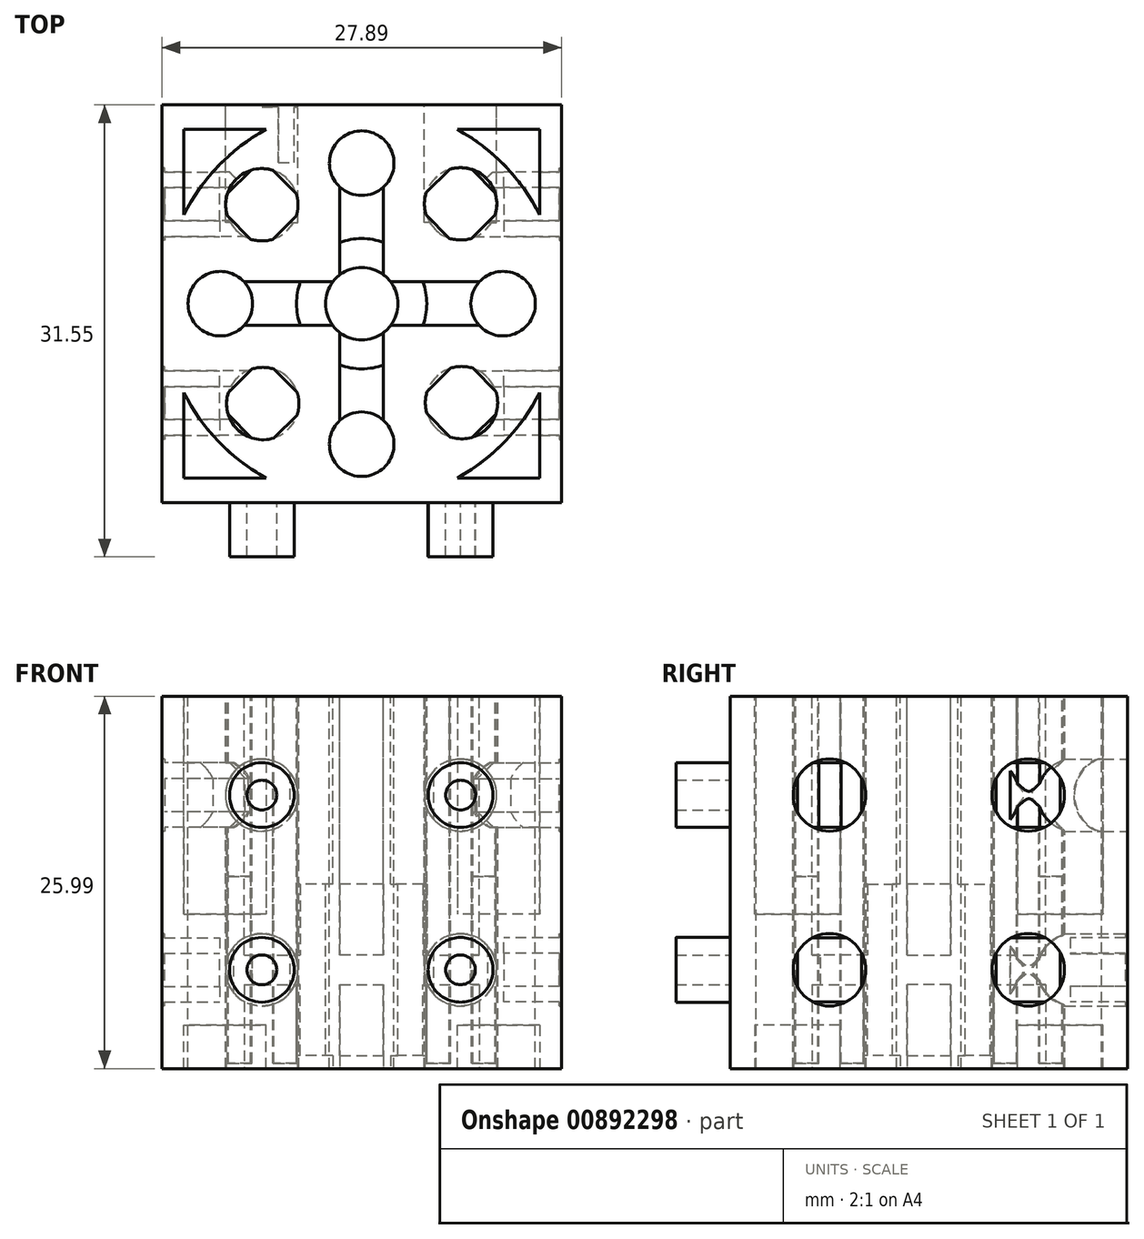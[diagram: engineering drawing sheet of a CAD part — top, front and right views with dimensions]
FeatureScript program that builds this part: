
annotation { "Feature Type Name" : "Feature", "Feature Type Description" : "" }
export const myFeature = defineFeature(function(context is Context, id is Id, definition is map)
    precondition{}
    {
        {
            var Q0;
            Q0=qCreatedBy(makeId("Top.planeOp"),FACE);
            var sketch = newSketch(context, id + "F0", { "sketchPlane" : qUnion([Q0])});
            skLineSegment(sketch, "E0.bottom", {"start": v(-12.61, 9.27) * mm, "end": v(15.28, 9.27) * mm});
            skLineSegment(sketch, "E0.top", {"start": v(-12.61, -18.5) * mm, "end": v(15.28, -18.5) * mm});
            skLineSegment(sketch, "E0.left", {"start": v(-12.61, 9.27) * mm, "end": v(-12.61, -18.5) * mm});
            skLineSegment(sketch, "E0.right", {"start": v(15.28, 9.27) * mm, "end": v(15.28, -18.5) * mm});
            skSolve(sketch);
        }
        {
            var Q0;
            Q0=qSketchRegion(id+"F0",true);
            extrude(context, id + "F1", {"entities" : qUnion([Q0]), "depth" : 13.8 * mm, "offsetDistance" : 25.4 * mm});
        }
        {
            var Q0;
            Q0=makeQuery(id+"F1.opExtrude","CAP_FACE",FACE,{"disambiguationData":[OSD([sQuery(id+"F0.wireOp",EDGE,"E0.bottom"),sQuery(id+"F0.wireOp",EDGE,"E0.top"),sQuery(id+"F0.wireOp",EDGE,"E0.left"),sQuery(id+"F0.wireOp",EDGE,"E0.right")])],"isStart":false});
            var sketch = newSketch(context, id + "F2", { "sketchPlane" : qUnion([Q0])});
            skLineSegment(sketch, "E1", {"start": v(1.33, 9.27) * mm, "end": v(1.33, -18.5) * mm, "construction": true});
            skLineSegment(sketch, "E2", {"start": v(-12.61, -4.61) * mm, "end": v(15.28, -4.61) * mm, "construction": true});
            skLineSegment(sketch, "E3.bottom", {"start": v(13.75, 7.56) * mm, "end": v(-11.09, 7.56) * mm});
            skLineSegment(sketch, "E3.top", {"start": v(13.75, -16.78) * mm, "end": v(-11.09, -16.78) * mm});
            skLineSegment(sketch, "E3.left", {"start": v(13.75, 7.56) * mm, "end": v(13.75, -16.78) * mm});
            skLineSegment(sketch, "E3.right", {"start": v(-11.09, 7.56) * mm, "end": v(-11.09, -16.78) * mm});
            skPoint(sketch, "E3.middle", {"position": v(1.33, -4.61) * mm});
            skSolve(sketch);
        }
        {
            var Q0;
            Q0=qSketchRegion(id+"F2",true);
            extrude(context, id + "F3", {"entities" : qUnion([Q0]), "operationType" : NewBodyOperationType.REMOVE, "oppositeDirection" : true, "depth" : 3.02 * mm, "offsetDistance" : 25.4 * mm});
        }
        {
            var Q0;
            Q0=makeQuery(id+"F1.opExtrude","CAP_FACE",FACE,{"disambiguationData":[OSD([sQuery(id+"F0.wireOp",EDGE,"E0.bottom"),sQuery(id+"F0.wireOp",EDGE,"E0.top"),sQuery(id+"F0.wireOp",EDGE,"E0.left"),sQuery(id+"F0.wireOp",EDGE,"E0.right")])],"isStart":true});
            var sketch = newSketch(context, id + "F4", { "sketchPlane" : qUnion([Q0])});
            skLineSegment(sketch, "E4.bottom", {"start": v(-11.09, -7.56) * mm, "end": v(13.75, -7.56) * mm});
            skLineSegment(sketch, "E4.top", {"start": v(-11.09, 16.78) * mm, "end": v(13.75, 16.78) * mm});
            skLineSegment(sketch, "E4.left", {"start": v(-11.09, -7.56) * mm, "end": v(-11.09, 16.78) * mm});
            skLineSegment(sketch, "E4.right", {"start": v(13.75, -7.56) * mm, "end": v(13.75, 16.78) * mm});
            skSolve(sketch);
        }
        {
            var Q0;
            Q0=makeQuery(id+"F4.imprint","IMPRINT",FACE,{"disambiguationData":[TD([[makeQuery(id+"F4.imprint","IMPRINT",EDGE,{"derivedFrom":sQuery(id+"F4.wireOp",EDGE,"E4.bottom")}),1.0]])]});
            extrude(context, id + "F5", {"entities" : qUnion([Q0]), "operationType" : NewBodyOperationType.REMOVE, "oppositeDirection" : true, "depth" : 3.02 * mm, "offsetDistance" : 25.4 * mm});
        }
        {
            var Q0;
            Q0=makeQuery(id+"F5.boolean.opBoolean","COPY",FACE,{"derivedFrom":makeQuery(id+"F5.opExtrude","CAP_FACE",FACE,{"disambiguationData":[OSD([sQuery(id+"F4.wireOp",EDGE,"E4.bottom"),sQuery(id+"F4.wireOp",EDGE,"E4.top"),sQuery(id+"F4.wireOp",EDGE,"E4.left"),sQuery(id+"F4.wireOp",EDGE,"E4.right")])],"isStart":false})});
            var sketch = newSketch(context, id + "F6", { "sketchPlane" : qUnion([Q0])});
            skCircle(sketch, "E5", {"center": v(1.33, 4.61) * mm, "radius": 13.88 * mm});
            skLineSegment(sketch, "E6", {"start": v(1.33, -7.56) * mm, "end": v(1.33, 16.78) * mm, "construction": true});
            skPoint(sketch, "E6.startSnap0", {"position": v(1.33, -7.56) * mm});
            skSolve(sketch);
        }
        {
            var Q0;
            {var subQ0=sQuery(id+"F6.wireOp",EDGE,"E5");var subQ1=makeQuery(id+"F5.boolean.opBoolean","COPY",EDGE,{"derivedFrom":makeQuery(id+"F5.opExtrude","CAP_EDGE",EDGE,{"disambiguationData":[OSD([sQuery(id+"F4.wireOp",EDGE,"E4.top")])],"isStart":false})});var subQ2=makeQuery(id+"F6.imprint","INTERSECT",VERTEX,{"disambiguationData":[OD(0.0)],"derivedFrom":[subQ1,subQ0]});Q0=makeQuery(id+"F6.imprint","IMPRINT",FACE,{"disambiguationData":[TD([[makeQuery(id+"F6.imprint","IMPRINT",EDGE,{"disambiguationData":[TD([[subQ2,-1.0]])],"derivedFrom":subQ0}),1.0]])]});}
            var Q1;
            {var subQ0=sQuery(id+"F6.wireOp",EDGE,"E5");var subQ1=makeQuery(id+"F5.boolean.opBoolean","COPY",EDGE,{"derivedFrom":makeQuery(id+"F5.opExtrude","CAP_EDGE",EDGE,{"disambiguationData":[OSD([sQuery(id+"F4.wireOp",EDGE,"E4.left")])],"isStart":false})});var subQ2=makeQuery(id+"F6.imprint","INTERSECT",VERTEX,{"disambiguationData":[OD(0.0)],"derivedFrom":[subQ1,subQ0]});Q1=makeQuery(id+"F6.imprint","IMPRINT",FACE,{"disambiguationData":[TD([[makeQuery(id+"F6.imprint","IMPRINT",EDGE,{"disambiguationData":[TD([[subQ2,-1.0]])],"derivedFrom":subQ0}),1.0]])]});}
            var Q2;
            {var subQ0=sQuery(id+"F6.wireOp",EDGE,"E5");var subQ1=makeQuery(id+"F5.boolean.opBoolean","COPY",EDGE,{"derivedFrom":makeQuery(id+"F5.opExtrude","CAP_EDGE",EDGE,{"disambiguationData":[OSD([sQuery(id+"F4.wireOp",EDGE,"E4.bottom")])],"isStart":false})});var subQ2=makeQuery(id+"F6.imprint","INTERSECT",VERTEX,{"disambiguationData":[OD(0.0)],"derivedFrom":[subQ1,subQ0]});Q2=makeQuery(id+"F6.imprint","IMPRINT",FACE,{"disambiguationData":[TD([[makeQuery(id+"F6.imprint","IMPRINT",EDGE,{"disambiguationData":[TD([[subQ2,-1.0]])],"derivedFrom":subQ0}),1.0]])]});}
            var Q3;
            {var subQ0=sQuery(id+"F6.wireOp",EDGE,"E5");var subQ1=makeQuery(id+"F5.boolean.opBoolean","COPY",EDGE,{"derivedFrom":makeQuery(id+"F5.opExtrude","CAP_EDGE",EDGE,{"disambiguationData":[OSD([sQuery(id+"F4.wireOp",EDGE,"E4.right")])],"isStart":false})});var subQ2=makeQuery(id+"F6.imprint","INTERSECT",VERTEX,{"disambiguationData":[OD(0.0)],"derivedFrom":[subQ1,subQ0]});Q3=makeQuery(id+"F6.imprint","IMPRINT",FACE,{"disambiguationData":[TD([[makeQuery(id+"F6.imprint","IMPRINT",EDGE,{"disambiguationData":[TD([[subQ2,1.0]])],"derivedFrom":subQ0}),1.0]])]});}
            var Q4;
            {var subQ0=sQuery(id+"F6.wireOp",EDGE,"E5");var subQ8=makeQuery(id+"F5.boolean.opBoolean","COPY",EDGE,{"derivedFrom":makeQuery(id+"F5.opExtrude","CAP_EDGE",EDGE,{"disambiguationData":[OSD([sQuery(id+"F4.wireOp",EDGE,"E4.top")])],"isStart":false})});var subQ11=makeQuery(id+"F6.imprint","INTERSECT",VERTEX,{"disambiguationData":[OD(0.0)],"derivedFrom":[subQ8,subQ0]});Q4=makeQuery(id+"F6.imprint","IMPRINT",FACE,{"disambiguationData":[TD([[makeQuery(id+"F6.imprint","IMPRINT",EDGE,{"disambiguationData":[TD([[subQ11,1.0]])],"derivedFrom":subQ0}),1.0]])]});}
            extrude(context, id + "F7", {"entities" : qUnion([Q0, Q1, Q2, Q3, Q4]), "operationType" : NewBodyOperationType.ADD, "depth" : 3.02 * mm, "offsetDistance" : 25.4 * mm});
        }
        {
            var Q0;
            Q0=makeQuery(id+"F3.boolean.opBoolean","COPY",FACE,{"derivedFrom":makeQuery(id+"F3.opExtrude","CAP_FACE",FACE,{"disambiguationData":[OSD([sQuery(id+"F2.wireOp",EDGE,"E3.bottom"),sQuery(id+"F2.wireOp",EDGE,"E3.top"),sQuery(id+"F2.wireOp",EDGE,"E3.left"),sQuery(id+"F2.wireOp",EDGE,"E3.right")])],"isStart":false})});
            var sketch = newSketch(context, id + "F8", { "sketchPlane" : qUnion([Q0])});
            skLineSegment(sketch, "E7", {"start": v(1.33, 7.56) * mm, "end": v(1.33, -16.78) * mm, "construction": true});
            skCircle(sketch, "E8", {"center": v(1.33, -4.61) * mm, "radius": 13.88 * mm});
            skSolve(sketch);
        }
        {
            var Q0;
            Q0=qSketchRegion(id+"F8",true);
            extrude(context, id + "F9", {"entities" : qUnion([Q0]), "operationType" : NewBodyOperationType.ADD, "depth" : 3.02 * mm, "offsetDistance" : 25.4 * mm});
        }
        {
            var Q0;
            Q0=makeQuery(id+"F9.boolean.opBoolean","MERGE",FACE,{"derivedFrom":[makeQuery(id+"F1.opExtrude","CAP_FACE",FACE,{"disambiguationData":[OSD([sQuery(id+"F0.wireOp",EDGE,"E0.bottom"),sQuery(id+"F0.wireOp",EDGE,"E0.top"),sQuery(id+"F0.wireOp",EDGE,"E0.left"),sQuery(id+"F0.wireOp",EDGE,"E0.right")])],"isStart":false}),makeQuery(id+"F9.opExtrude","CAP_FACE",FACE,{"disambiguationData":[OSD([sQuery(id+"F8.wireOp",EDGE,"E8")])],"isStart":false})]});
            var sketch = newSketch(context, id + "F10", { "sketchPlane" : qUnion([Q0])});
            skLineSegment(sketch, "E9", {"start": v(-12.61, -4.61) * mm, "end": v(15.28, -4.61) * mm, "construction": true});
            skLineSegment(sketch, "E10", {"start": v(1.33, 9.27) * mm, "end": v(1.33, -18.5) * mm, "construction": true});
            skCircle(sketch, "E11", {"center": v(1.33, -4.61) * mm, "radius": 2.53 * mm});
            skCircle(sketch, "E12", {"center": v(1.33, -14.42) * mm, "radius": 2.25 * mm});
            skCircle(sketch, "E13", {"center": v(1.33, 5.2) * mm, "radius": 2.25 * mm});
            skCircle(sketch, "E14", {"center": v(-8.54, -4.61) * mm, "radius": 2.25 * mm});
            skCircle(sketch, "E15", {"center": v(11.2, -4.61) * mm, "radius": 2.25 * mm});
            skCircle(sketch, "E16", {"center": v(-5.64, 2.3) * mm, "radius": 2.53 * mm});
            skCircle(sketch, "E17.1.0", {"center": v(-5.57, -11.58) * mm, "radius": 2.53 * mm});
            skCircle(sketch, "E17.2.0", {"center": v(8.3, -11.52) * mm, "radius": 2.53 * mm});
            skCircle(sketch, "E17.3.0", {"center": v(8.24, 2.36) * mm, "radius": 2.53 * mm});
            skSolve(sketch);
        }
        {
            var Q0;
            Q0=qSketchRegion(id+"F10",true);
            extrude(context, id + "F11", {"entities" : qUnion([Q0]), "operationType" : NewBodyOperationType.REMOVE, "oppositeDirection" : true, "depth" : 25.4 * mm, "offsetDistance" : 25.4 * mm});
        }
        {
            var Q0;
            Q0=makeQuery(id+"F9.boolean.opBoolean","MERGE",FACE,{"derivedFrom":[makeQuery(id+"F1.opExtrude","CAP_FACE",FACE,{"disambiguationData":[OSD([sQuery(id+"F0.wireOp",EDGE,"E0.bottom"),sQuery(id+"F0.wireOp",EDGE,"E0.top"),sQuery(id+"F0.wireOp",EDGE,"E0.left"),sQuery(id+"F0.wireOp",EDGE,"E0.right")])],"isStart":false}),makeQuery(id+"F9.opExtrude","CAP_FACE",FACE,{"disambiguationData":[OSD([sQuery(id+"F8.wireOp",EDGE,"E8")])],"isStart":false})]});
            var sketch = newSketch(context, id + "F12", { "sketchPlane" : qUnion([Q0])});
            skLineSegment(sketch, "E18", {"start": v(-12.61, -4.61) * mm, "end": v(15.28, -4.61) * mm, "construction": true});
            skLineSegment(sketch, "E19", {"start": v(1.33, 9.27) * mm, "end": v(1.33, -18.5) * mm, "construction": true});
            skLineSegment(sketch, "E20", {"start": v(-6.88, -3.09) * mm, "end": v(9.55, -3.09) * mm});
            skLineSegment(sketch, "E21", {"start": v(-6.88, -6.14) * mm, "end": v(9.55, -6.14) * mm});
            skLineSegment(sketch, "E22", {"start": v(-0.19, 3.54) * mm, "end": v(-0.19, -12.76) * mm});
            skLineSegment(sketch, "E23", {"start": v(2.86, -12.76) * mm, "end": v(2.86, 3.54) * mm});
            skLineSegment(sketch, "E24", {"start": v(-0.19, -7.96) * mm, "end": v(2.86, -7.96) * mm, "construction": true});
            skPoint(sketch, "E25", {"position": v(1.33, -7.96) * mm});
            skLineSegment(sketch, "E26", {"start": v(-2, -3.09) * mm, "end": v(-2, -6.14) * mm, "construction": true});
            skPoint(sketch, "E27", {"position": v(-2, -4.61) * mm});
            skSolve(sketch);
        }
        {
            var Q0;
            {var subQ0=sQuery(id+"F12.wireOp",EDGE,"E22");var subQ1=makeQuery(id+"F11.boolean.opBoolean","COPY",EDGE,{"derivedFrom":makeQuery(id+"F11.opExtrude","CAP_EDGE",EDGE,{"disambiguationData":[OSD([sQuery(id+"F10.wireOp",EDGE,"E13")])],"isStart":true})});var subQ2=makeQuery(id+"F12.imprint","INTERSECT",VERTEX,{"derivedFrom":[subQ1,subQ0]});Q0=makeQuery(id+"F12.imprint","IMPRINT",FACE,{"disambiguationData":[TD([[makeQuery(id+"F12.imprint","IMPRINT",EDGE,{"disambiguationData":[TD([[subQ2,-1.0]])],"derivedFrom":subQ0}),1.0]])]});}
            var Q1;
            {var subQ0=sQuery(id+"F12.wireOp",EDGE,"E22");var subQ1=makeQuery(id+"F11.boolean.opBoolean","COPY",EDGE,{"derivedFrom":makeQuery(id+"F11.opExtrude","CAP_EDGE",EDGE,{"disambiguationData":[OSD([sQuery(id+"F10.wireOp",EDGE,"E12")])],"isStart":true})});var subQ2=makeQuery(id+"F12.imprint","INTERSECT",VERTEX,{"derivedFrom":[subQ1,subQ0]});Q1=makeQuery(id+"F12.imprint","IMPRINT",FACE,{"disambiguationData":[TD([[makeQuery(id+"F12.imprint","IMPRINT",EDGE,{"disambiguationData":[TD([[subQ2,1.0]])],"derivedFrom":subQ0}),1.0]])]});}
            var Q2;
            {var subQ0=sQuery(id+"F12.wireOp",EDGE,"E20");var subQ1=makeQuery(id+"F11.boolean.opBoolean","COPY",EDGE,{"derivedFrom":makeQuery(id+"F11.opExtrude","CAP_EDGE",EDGE,{"disambiguationData":[OSD([sQuery(id+"F10.wireOp",EDGE,"E14")])],"isStart":true})});var subQ2=makeQuery(id+"F12.imprint","INTERSECT",VERTEX,{"derivedFrom":[subQ1,subQ0]});Q2=makeQuery(id+"F12.imprint","IMPRINT",FACE,{"disambiguationData":[TD([[makeQuery(id+"F12.imprint","IMPRINT",EDGE,{"disambiguationData":[TD([[subQ2,-1.0]])],"derivedFrom":subQ0}),-1.0]])]});}
            var Q3;
            {var subQ0=sQuery(id+"F12.wireOp",EDGE,"E20");var subQ1=makeQuery(id+"F11.boolean.opBoolean","COPY",EDGE,{"derivedFrom":makeQuery(id+"F11.opExtrude","CAP_EDGE",EDGE,{"disambiguationData":[OSD([sQuery(id+"F10.wireOp",EDGE,"E15")])],"isStart":true})});var subQ2=makeQuery(id+"F12.imprint","INTERSECT",VERTEX,{"derivedFrom":[subQ1,subQ0]});Q3=makeQuery(id+"F12.imprint","IMPRINT",FACE,{"disambiguationData":[TD([[makeQuery(id+"F12.imprint","IMPRINT",EDGE,{"disambiguationData":[TD([[subQ2,1.0]])],"derivedFrom":subQ0}),-1.0]])]});}
            extrude(context, id + "F13", {"entities" : qUnion([Q0, Q1, Q2, Q3]), "operationType" : NewBodyOperationType.REMOVE, "oppositeDirection" : true, "depth" : 5.87 * mm, "offsetDistance" : 25.4 * mm});
        }
        {
            var Q0;
            Q0=makeQuery(id+"F7.boolean.opBoolean","MERGE",FACE,{"derivedFrom":[makeQuery(id+"F1.opExtrude","CAP_FACE",FACE,{"disambiguationData":[OSD([sQuery(id+"F0.wireOp",EDGE,"E0.bottom"),sQuery(id+"F0.wireOp",EDGE,"E0.top"),sQuery(id+"F0.wireOp",EDGE,"E0.left"),sQuery(id+"F0.wireOp",EDGE,"E0.right")])],"isStart":true}),makeQuery(id+"F7.opExtrude","CAP_FACE",FACE,{"disambiguationData":[OSD([sQuery(id+"F6.wireOp",EDGE,"E5")])],"isStart":false})]});
            var sketch = newSketch(context, id + "F14", { "sketchPlane" : qUnion([Q0])});
            skLineSegment(sketch, "E28.0", {"start": v(2.86, 12.76) * mm, "end": v(2.86, 6.63) * mm});
            skLineSegment(sketch, "E28.1", {"start": v(3.35, 6.14) * mm, "end": v(9.55, 6.14) * mm});
            skLineSegment(sketch, "E28.2", {"start": v(3.35, 3.09) * mm, "end": v(9.55, 3.09) * mm});
            skLineSegment(sketch, "E28.3", {"start": v(2.86, 2.6) * mm, "end": v(2.86, -3.54) * mm});
            skLineSegment(sketch, "E28.4", {"start": v(-0.19, -3.54) * mm, "end": v(-0.19, 2.6) * mm});
            skLineSegment(sketch, "E28.5", {"start": v(-0.19, 6.63) * mm, "end": v(-0.19, 12.76) * mm});
            skLineSegment(sketch, "E28.6", {"start": v(-6.88, 6.14) * mm, "end": v(-0.68, 6.14) * mm});
            skLineSegment(sketch, "E28.7", {"start": v(-6.88, 3.09) * mm, "end": v(-0.68, 3.09) * mm});
            skSolve(sketch);
        }
        {
            var Q0;
            {var subQ0=sQuery(id+"F14.wireOp",EDGE,"E28.6");Q0=makeQuery(id+"F14.imprint","IMPRINT",FACE,{"disambiguationData":[TD([[makeQuery(id+"F14.imprint","IMPRINT",EDGE,{"derivedFrom":subQ0}),-1.0]])]});}
            var Q1;
            {var subQ0=sQuery(id+"F14.wireOp",EDGE,"E28.3");Q1=makeQuery(id+"F14.imprint","IMPRINT",FACE,{"disambiguationData":[TD([[makeQuery(id+"F14.imprint","IMPRINT",EDGE,{"derivedFrom":subQ0}),-1.0]])]});}
            var Q2;
            {var subQ0=sQuery(id+"F14.wireOp",EDGE,"E28.0");Q2=makeQuery(id+"F14.imprint","IMPRINT",FACE,{"disambiguationData":[TD([[makeQuery(id+"F14.imprint","IMPRINT",EDGE,{"derivedFrom":subQ0}),-1.0]])]});}
            var Q3;
            {var subQ0=sQuery(id+"F14.wireOp",EDGE,"E28.1");Q3=makeQuery(id+"F14.imprint","IMPRINT",FACE,{"disambiguationData":[TD([[makeQuery(id+"F14.imprint","IMPRINT",EDGE,{"derivedFrom":subQ0}),-1.0]])]});}
            extrude(context, id + "F15", {"entities" : qUnion([Q0, Q1, Q2, Q3]), "operationType" : NewBodyOperationType.REMOVE, "oppositeDirection" : true, "depth" : 5.87 * mm, "offsetDistance" : 25.4 * mm});
        }
        {
            var Q0;
            Q0=makeQuery(id+"F15.boolean.opBoolean","COPY",FACE,{"derivedFrom":makeQuery(id+"F15.opExtrude","CAP_FACE",FACE,{"disambiguationData":[OSD([sQuery(id+"F0.wireOp",EDGE,"E0.bottom"),sQuery(id+"F0.wireOp",EDGE,"E0.top"),sQuery(id+"F0.wireOp",EDGE,"E0.left"),sQuery(id+"F0.wireOp",EDGE,"E0.right"),sQuery(id+"F6.wireOp",EDGE,"E5"),sQuery(id+"F10.wireOp",EDGE,"E11"),sQuery(id+"F10.wireOp",EDGE,"E13"),sQuery(id+"F14.wireOp",EDGE,"E28.3"),sQuery(id+"F14.wireOp",EDGE,"E28.4")])],"isStart":false})});
            var sketch = newSketch(context, id + "F16", { "sketchPlane" : qUnion([Q0])});
            skCircle(sketch, "E29", {"center": v(1.33, 4.61) * mm, "radius": 4.55 * mm});
            skCircle(sketch, "E30", {"center": v(1.33, 4.61) * mm, "radius": 2.53 * mm});
            skSolve(sketch);
        }
        {
            var Q0;
            {var subQ5=sQuery(id+"F16.wireOp",EDGE,"E30");Q0=makeQuery(id+"F16.imprint","IMPRINT",FACE,{"disambiguationData":[TD([[makeQuery(id+"F16.imprint","IMPRINT",EDGE,{"disambiguationData":[OD(1.0)],"derivedFrom":subQ5}),-1.0]])]});}
            var Q1;
            {var subQ5=sQuery(id+"F16.wireOp",EDGE,"E30");Q1=makeQuery(id+"F16.imprint","IMPRINT",FACE,{"disambiguationData":[TD([[makeQuery(id+"F16.imprint","IMPRINT",EDGE,{"disambiguationData":[OD(0.0)],"derivedFrom":subQ5}),1.0]])]});}
            extrude(context, id + "F17", {"entities" : qUnion([Q0, Q1]), "operationType" : NewBodyOperationType.ADD, "depth" : 4.95 * mm, "offsetDistance" : 25.4 * mm});
        }
        {
            var Q0;
            Q0=makeQuery(id+"F13.boolean.opBoolean","COPY",FACE,{"derivedFrom":makeQuery(id+"F13.opExtrude","CAP_FACE",FACE,{"disambiguationData":[OSD([sQuery(id+"F10.wireOp",EDGE,"E11"),sQuery(id+"F10.wireOp",EDGE,"E12"),sQuery(id+"F12.wireOp",EDGE,"E22"),sQuery(id+"F12.wireOp",EDGE,"E23")])],"isStart":false})});
            var sketch = newSketch(context, id + "F18", { "sketchPlane" : qUnion([Q0])});
            skCircle(sketch, "E31", {"center": v(1.33, -4.61) * mm, "radius": 4.55 * mm});
            skCircle(sketch, "E32", {"center": v(1.33, -4.61) * mm, "radius": 2.53 * mm});
            skSolve(sketch);
        }
        {
            var Q0;
            {var subQ0=sQuery(id+"F18.wireOp",EDGE,"E31");var subQ1=sQuery(id+"F12.wireOp",EDGE,"E22");var subQ2=makeQuery(id+"F11.boolean.opBoolean","COPY",EDGE,{"derivedFrom":makeQuery(id+"F11.opExtrude","CAP_EDGE",EDGE,{"disambiguationData":[OSD([sQuery(id+"F10.wireOp",EDGE,"E12")])],"isStart":true})});var subQ4=makeQuery(id+"F13.boolean.opBoolean","COPY",EDGE,{"derivedFrom":makeQuery(id+"F13.opExtrude","CAP_EDGE",EDGE,{"disambiguationData":[OSD([subQ1]),TDD([makeQuery(id+"F12.imprint","IMPRINT",EDGE,{"disambiguationData":[TD([[makeQuery(id+"F12.imprint","INTERSECT",VERTEX,{"derivedFrom":[subQ2,subQ1]}),1.0]])],"derivedFrom":subQ1})])],"isStart":false})});var subQ5=makeQuery(id+"F18.imprint","INTERSECT",VERTEX,{"derivedFrom":[subQ4,subQ0]});Q0=makeQuery(id+"F18.imprint","IMPRINT",FACE,{"disambiguationData":[TD([[makeQuery(id+"F18.imprint","IMPRINT",EDGE,{"disambiguationData":[TD([[subQ5,1.0]])],"derivedFrom":subQ0}),1.0]])]});}
            var Q1;
            {var subQ0=sQuery(id+"F18.wireOp",EDGE,"E31");var subQ1=sQuery(id+"F12.wireOp",EDGE,"E22");var subQ2=makeQuery(id+"F11.boolean.opBoolean","COPY",EDGE,{"derivedFrom":makeQuery(id+"F11.opExtrude","CAP_EDGE",EDGE,{"disambiguationData":[OSD([sQuery(id+"F10.wireOp",EDGE,"E12")])],"isStart":true})});var subQ4=makeQuery(id+"F13.boolean.opBoolean","COPY",EDGE,{"derivedFrom":makeQuery(id+"F13.opExtrude","CAP_EDGE",EDGE,{"disambiguationData":[OSD([subQ1]),TDD([makeQuery(id+"F12.imprint","IMPRINT",EDGE,{"disambiguationData":[TD([[makeQuery(id+"F12.imprint","INTERSECT",VERTEX,{"derivedFrom":[subQ2,subQ1]}),1.0]])],"derivedFrom":subQ1})])],"isStart":false})});var subQ5=makeQuery(id+"F18.imprint","INTERSECT",VERTEX,{"derivedFrom":[subQ4,subQ0]});Q1=makeQuery(id+"F18.imprint","IMPRINT",FACE,{"disambiguationData":[TD([[makeQuery(id+"F18.imprint","IMPRINT",EDGE,{"disambiguationData":[TD([[subQ5,-1.0]])],"derivedFrom":subQ0}),1.0]])]});}
            extrude(context, id + "F19", {"entities" : qUnion([Q0, Q1]), "operationType" : NewBodyOperationType.ADD, "depth" : 4.95 * mm, "offsetDistance" : 25.4 * mm});
        }
        {
            var Q0;
            Q0=makeQuery(id+"F1.opExtrude","SWEPT_FACE",FACE,{"disambiguationData":[OSD([sQuery(id+"F0.wireOp",EDGE,"E0.top")])]});
            var sketch = newSketch(context, id + "F20", { "sketchPlane" : qUnion([Q0])});
            skLineSegment(sketch, "E33", {"start": v(15.28, 6.9) * mm, "end": v(-12.61, 6.9) * mm, "construction": true});
            skCircle(sketch, "E34", {"center": v(8.23, 6.9) * mm, "radius": 2.26 * mm});
            skCircle(sketch, "E35", {"center": v(-5.64, 6.9) * mm, "radius": 2.26 * mm});
            skLineSegment(sketch, "E36", {"start": v(1.33, 0) * mm, "end": v(1.33, 13.8) * mm, "construction": true});
            skPoint(sketch, "E37", {"position": v(1.33, 6.9) * mm});
            skLineSegment(sketch, "E38", {"start": v(1.33, 0) * mm, "end": v(15.28, 0) * mm, "construction": true});
            skLineSegment(sketch, "E39", {"start": v(15.28, 0) * mm, "end": v(8.3, 0) * mm});
            skLineSegment(sketch, "E40", {"start": v(8.3, 0) * mm, "end": v(8.3, 13.8) * mm, "construction": true});
            skLineSegment(sketch, "E41", {"start": v(1.33, 0) * mm, "end": v(-12.61, 0) * mm, "construction": true});
            skLineSegment(sketch, "E42", {"start": v(-5.64, 0) * mm, "end": v(-5.64, 13.8) * mm, "construction": true});
            skCircle(sketch, "E43", {"center": v(8.23, 6.9) * mm, "radius": 1.04 * mm});
            skCircle(sketch, "E44", {"center": v(-5.64, 6.9) * mm, "radius": 1.04 * mm});
            skLineSegment(sketch, "E45.0", {"start": v(-12.61, 13.8) * mm, "end": v(-12.61, 0) * mm});
            skSolve(sketch);
        }
        {
            var Q0;
            Q0=makeQuery(id+"F20.imprint","IMPRINT",FACE,{"disambiguationData":[TD([[makeQuery(id+"F20.imprint","IMPRINT",EDGE,{"derivedFrom":sQuery(id+"F20.wireOp",EDGE,"E34")}),1.0]])]});
            var Q1;
            Q1=makeQuery(id+"F20.imprint","IMPRINT",FACE,{"disambiguationData":[TD([[makeQuery(id+"F20.imprint","IMPRINT",EDGE,{"derivedFrom":sQuery(id+"F20.wireOp",EDGE,"E35")}),1.0]])]});
            extrude(context, id + "F21", {"entities" : qUnion([Q0, Q1]), "operationType" : NewBodyOperationType.ADD, "depth" : 3.78 * mm, "offsetDistance" : 25.4 * mm});
        }
        {
            var Q0;
            Q0=makeQuery(id+"F1.opExtrude","SWEPT_FACE",FACE,{"disambiguationData":[OSD([sQuery(id+"F0.wireOp",EDGE,"E0.bottom")])]});
            var sketch = newSketch(context, id + "F22", { "sketchPlane" : qUnion([Q0])});
            skCircle(sketch, "E46.0", {"center": v(-8.23, 6.9) * mm, "radius": 2.26 * mm, "construction": true});
            skCircle(sketch, "E46.1", {"center": v(5.64, 6.9) * mm, "radius": 2.26 * mm, "construction": true});
            skCircle(sketch, "E47", {"center": v(-8.23, 6.9) * mm, "radius": 2.53 * mm});
            skCircle(sketch, "E48", {"center": v(5.64, 6.9) * mm, "radius": 2.53 * mm});
            skSolve(sketch);
        }
        {
            var Q0;
            Q0=qSketchRegion(id+"F22",true);
            extrude(context, id + "F23", {"entities" : qUnion([Q0]), "operationType" : NewBodyOperationType.REMOVE, "oppositeDirection" : true, "depth" : 4 * mm, "offsetDistance" : 25.4 * mm});
        }
        {
            var Q0;
            Q0=makeQuery(id+"F1.opExtrude","SWEPT_FACE",FACE,{"disambiguationData":[OSD([sQuery(id+"F0.wireOp",EDGE,"E0.right")])]});
            var sketch = newSketch(context, id + "F24", { "sketchPlane" : qUnion([Q0])});
            skLineSegment(sketch, "E49", {"start": v(9.27, 6.9) * mm, "end": v(-18.5, 6.9) * mm, "construction": true});
            skLineSegment(sketch, "E50", {"start": v(-4.61, 13.8) * mm, "end": v(-4.61, 0) * mm});
            skLineSegment(sketch, "E51", {"start": v(-4.61, 13.8) * mm, "end": v(9.27, 13.8) * mm, "construction": true});
            skLineSegment(sketch, "E52", {"start": v(-4.61, 13.8) * mm, "end": v(-18.5, 13.8) * mm, "construction": true});
            skLineSegment(sketch, "E53", {"start": v(-11.55, 13.8) * mm, "end": v(-11.55, 0) * mm, "construction": true});
            skLineSegment(sketch, "E54", {"start": v(2.33, 13.8) * mm, "end": v(2.33, 0) * mm, "construction": true});
            skPoint(sketch, "E55", {"position": v(-11.55, 6.9) * mm});
            skPoint(sketch, "E56", {"position": v(2.33, 6.9) * mm});
            skCircle(sketch, "E57", {"center": v(-11.55, 6.9) * mm, "radius": 2.53 * mm});
            skCircle(sketch, "E58", {"center": v(2.33, 6.9) * mm, "radius": 2.53 * mm});
            skSolve(sketch);
        }
        {
            var Q0;
            Q0=qSketchRegion(id+"F24",true);
            extrude(context, id + "F25", {"entities" : qUnion([Q0]), "operationType" : NewBodyOperationType.REMOVE, "oppositeDirection" : true, "depth" : 4 * mm, "offsetDistance" : 25.4 * mm});
        }
        {
            var Q0;
            Q0=makeQuery(id+"F1.opExtrude","SWEPT_FACE",FACE,{"disambiguationData":[OSD([sQuery(id+"F0.wireOp",EDGE,"E0.left")])]});
            var sketch = newSketch(context, id + "F26", { "sketchPlane" : qUnion([Q0])});
            skCircle(sketch, "E59.0", {"center": v(-2.33, 6.9) * mm, "radius": 2.53 * mm});
            skCircle(sketch, "E59.1", {"center": v(11.55, 6.9) * mm, "radius": 2.53 * mm});
            skSolve(sketch);
        }
        {
            var Q0;
            Q0=qSketchRegion(id+"F26",true);
            extrude(context, id + "F27", {"entities" : qUnion([Q0]), "operationType" : NewBodyOperationType.REMOVE, "oppositeDirection" : true, "depth" : 4 * mm, "offsetDistance" : 25.4 * mm});
        }
        {
            var Q0;
            Q0=makeQuery(id+"F23.boolean.opBoolean","COPY",FACE,{"derivedFrom":makeQuery(id+"F23.opExtrude","CAP_FACE",FACE,{"disambiguationData":[OSD([sQuery(id+"F22.wireOp",EDGE,"E47")])],"isStart":false})});
            var sketch = newSketch(context, id + "F28", { "sketchPlane" : qUnion([Q0])});
            skLineSegment(sketch, "E60.bottom", {"start": v(-5.98, 9.14) * mm, "end": v(-10.48, 9.14) * mm});
            skLineSegment(sketch, "E60.top", {"start": v(-5.98, 4.65) * mm, "end": v(-10.48, 4.65) * mm});
            skLineSegment(sketch, "E60.left", {"start": v(-5.98, 9.14) * mm, "end": v(-5.98, 4.65) * mm});
            skLineSegment(sketch, "E60.right", {"start": v(-10.48, 9.14) * mm, "end": v(-10.48, 4.65) * mm});
            skPoint(sketch, "E60.middle", {"position": v(-8.23, 6.9) * mm});
            skLineSegment(sketch, "E61.bottom", {"start": v(7.89, 9.14) * mm, "end": v(3.4, 9.14) * mm});
            skLineSegment(sketch, "E61.top", {"start": v(7.89, 4.65) * mm, "end": v(3.4, 4.65) * mm});
            skLineSegment(sketch, "E61.left", {"start": v(7.89, 9.14) * mm, "end": v(7.89, 4.65) * mm});
            skLineSegment(sketch, "E61.right", {"start": v(3.4, 9.14) * mm, "end": v(3.4, 4.65) * mm});
            skPoint(sketch, "E61.middle", {"position": v(5.64, 6.9) * mm});
            skCircle(sketch, "E62.0", {"center": v(-8.23, 6.9) * mm, "radius": 2.53 * mm});
            skCircle(sketch, "E63.0", {"center": v(5.64, 6.9) * mm, "radius": 2.53 * mm});
            skSolve(sketch);
        }
        {
            var Q0;
            {var subQ0=sQuery(id+"F28.wireOp",EDGE,"E62.0");var subQ1=sQuery(id+"F28.wireOp",EDGE,"E60.right");var subQ2=makeQuery(id+"F28.imprint","INTERSECT",VERTEX,{"disambiguationData":[OD(0.0)],"derivedFrom":[subQ1,subQ0]});Q0=makeQuery(id+"F28.imprint","IMPRINT",FACE,{"disambiguationData":[TD([[makeQuery(id+"F28.imprint","IMPRINT",EDGE,{"disambiguationData":[TD([[subQ2,-1.0]])],"derivedFrom":subQ1}),-1.0]])]});}
            var Q1;
            {var subQ0=sQuery(id+"F28.wireOp",EDGE,"E62.0");var subQ1=sQuery(id+"F28.wireOp",EDGE,"E60.top");var subQ2=makeQuery(id+"F28.imprint","INTERSECT",VERTEX,{"disambiguationData":[OD(0.0)],"derivedFrom":[subQ1,subQ0]});Q1=makeQuery(id+"F28.imprint","IMPRINT",FACE,{"disambiguationData":[TD([[makeQuery(id+"F28.imprint","IMPRINT",EDGE,{"disambiguationData":[TD([[subQ2,-1.0]])],"derivedFrom":subQ1}),1.0]])]});}
            var Q2;
            {var subQ0=sQuery(id+"F28.wireOp",EDGE,"E62.0");var subQ1=sQuery(id+"F28.wireOp",EDGE,"E60.left");var subQ2=makeQuery(id+"F28.imprint","INTERSECT",VERTEX,{"disambiguationData":[OD(0.0)],"derivedFrom":[subQ1,subQ0]});Q2=makeQuery(id+"F28.imprint","IMPRINT",FACE,{"disambiguationData":[TD([[makeQuery(id+"F28.imprint","IMPRINT",EDGE,{"disambiguationData":[TD([[subQ2,-1.0]])],"derivedFrom":subQ1}),1.0]])]});}
            var Q3;
            {var subQ0=sQuery(id+"F28.wireOp",EDGE,"E62.0");var subQ1=sQuery(id+"F28.wireOp",EDGE,"E60.bottom");var subQ2=makeQuery(id+"F28.imprint","INTERSECT",VERTEX,{"disambiguationData":[OD(0.0)],"derivedFrom":[subQ1,subQ0]});Q3=makeQuery(id+"F28.imprint","IMPRINT",FACE,{"disambiguationData":[TD([[makeQuery(id+"F28.imprint","IMPRINT",EDGE,{"disambiguationData":[TD([[subQ2,-1.0]])],"derivedFrom":subQ1}),-1.0]])]});}
            var Q4;
            {var subQ0=sQuery(id+"F28.wireOp",EDGE,"E63.0");var subQ1=sQuery(id+"F28.wireOp",EDGE,"E61.bottom");var subQ2=makeQuery(id+"F28.imprint","INTERSECT",VERTEX,{"disambiguationData":[OD(0.0)],"derivedFrom":[subQ1,subQ0]});Q4=makeQuery(id+"F28.imprint","IMPRINT",FACE,{"disambiguationData":[TD([[makeQuery(id+"F28.imprint","IMPRINT",EDGE,{"disambiguationData":[TD([[subQ2,-1.0]])],"derivedFrom":subQ1}),-1.0]])]});}
            var Q5;
            {var subQ0=sQuery(id+"F28.wireOp",EDGE,"E63.0");var subQ1=sQuery(id+"F28.wireOp",EDGE,"E61.left");var subQ2=makeQuery(id+"F28.imprint","INTERSECT",VERTEX,{"disambiguationData":[OD(0.0)],"derivedFrom":[subQ1,subQ0]});Q5=makeQuery(id+"F28.imprint","IMPRINT",FACE,{"disambiguationData":[TD([[makeQuery(id+"F28.imprint","IMPRINT",EDGE,{"disambiguationData":[TD([[subQ2,-1.0]])],"derivedFrom":subQ1}),1.0]])]});}
            var Q6;
            {var subQ0=sQuery(id+"F28.wireOp",EDGE,"E63.0");var subQ1=sQuery(id+"F28.wireOp",EDGE,"E61.right");var subQ2=makeQuery(id+"F28.imprint","INTERSECT",VERTEX,{"disambiguationData":[OD(0.0)],"derivedFrom":[subQ1,subQ0]});Q6=makeQuery(id+"F28.imprint","IMPRINT",FACE,{"disambiguationData":[TD([[makeQuery(id+"F28.imprint","IMPRINT",EDGE,{"disambiguationData":[TD([[subQ2,-1.0]])],"derivedFrom":subQ1}),-1.0]])]});}
            var Q7;
            {var subQ0=sQuery(id+"F28.wireOp",EDGE,"E63.0");var subQ1=sQuery(id+"F28.wireOp",EDGE,"E61.top");var subQ2=makeQuery(id+"F28.imprint","INTERSECT",VERTEX,{"disambiguationData":[OD(0.0)],"derivedFrom":[subQ1,subQ0]});Q7=makeQuery(id+"F28.imprint","IMPRINT",FACE,{"disambiguationData":[TD([[makeQuery(id+"F28.imprint","IMPRINT",EDGE,{"disambiguationData":[TD([[subQ2,-1.0]])],"derivedFrom":subQ1}),1.0]])]});}
            extrude(context, id + "F29", {"entities" : qUnion([Q0, Q1, Q2, Q3, Q4, Q5, Q6, Q7]), "operationType" : NewBodyOperationType.ADD, "depth" : 3.86 * mm, "offsetDistance" : 25.4 * mm});
        }
        {
            var Q0;
            Q0=makeQuery(id+"F25.boolean.opBoolean","COPY",FACE,{"derivedFrom":makeQuery(id+"F25.opExtrude","CAP_FACE",FACE,{"disambiguationData":[OSD([sQuery(id+"F24.wireOp",EDGE,"E57")])],"isStart":false})});
            var sketch = newSketch(context, id + "F30", { "sketchPlane" : qUnion([Q0])});
            skLineSegment(sketch, "E64.bottom", {"start": v(-9.3, 9.14) * mm, "end": v(-13.8, 9.14) * mm});
            skLineSegment(sketch, "E64.top", {"start": v(-9.3, 4.65) * mm, "end": v(-13.8, 4.65) * mm});
            skLineSegment(sketch, "E64.left", {"start": v(-9.3, 9.14) * mm, "end": v(-9.3, 4.65) * mm});
            skLineSegment(sketch, "E64.right", {"start": v(-13.8, 9.14) * mm, "end": v(-13.8, 4.65) * mm});
            skPoint(sketch, "E64.middle", {"position": v(-11.55, 6.9) * mm});
            skLineSegment(sketch, "E65.bottom", {"start": v(4.58, 9.14) * mm, "end": v(0.08, 9.14) * mm});
            skLineSegment(sketch, "E65.top", {"start": v(4.58, 4.65) * mm, "end": v(0.08, 4.65) * mm});
            skLineSegment(sketch, "E65.left", {"start": v(4.58, 9.14) * mm, "end": v(4.58, 4.65) * mm});
            skLineSegment(sketch, "E65.right", {"start": v(0.08, 9.14) * mm, "end": v(0.08, 4.65) * mm});
            skPoint(sketch, "E65.middle", {"position": v(2.33, 6.9) * mm});
            skCircle(sketch, "E66.0", {"center": v(-11.55, 6.9) * mm, "radius": 2.53 * mm});
            skCircle(sketch, "E66.1", {"center": v(2.33, 6.9) * mm, "radius": 2.53 * mm});
            skSolve(sketch);
        }
        {
            var Q0;
            {var subQ0=sQuery(id+"F30.wireOp",EDGE,"E66.0");var subQ1=sQuery(id+"F30.wireOp",EDGE,"E64.bottom");var subQ2=makeQuery(id+"F30.imprint","INTERSECT",VERTEX,{"disambiguationData":[OD(0.0)],"derivedFrom":[subQ1,subQ0]});Q0=makeQuery(id+"F30.imprint","IMPRINT",FACE,{"disambiguationData":[TD([[makeQuery(id+"F30.imprint","IMPRINT",EDGE,{"disambiguationData":[TD([[subQ2,-1.0]])],"derivedFrom":subQ1}),-1.0]])]});}
            var Q1;
            {var subQ0=sQuery(id+"F30.wireOp",EDGE,"E66.0");var subQ1=sQuery(id+"F30.wireOp",EDGE,"E64.right");var subQ2=makeQuery(id+"F30.imprint","INTERSECT",VERTEX,{"disambiguationData":[OD(0.0)],"derivedFrom":[subQ1,subQ0]});Q1=makeQuery(id+"F30.imprint","IMPRINT",FACE,{"disambiguationData":[TD([[makeQuery(id+"F30.imprint","IMPRINT",EDGE,{"disambiguationData":[TD([[subQ2,-1.0]])],"derivedFrom":subQ1}),-1.0]])]});}
            var Q2;
            {var subQ0=sQuery(id+"F30.wireOp",EDGE,"E66.0");var subQ1=sQuery(id+"F30.wireOp",EDGE,"E64.left");var subQ2=makeQuery(id+"F30.imprint","INTERSECT",VERTEX,{"disambiguationData":[OD(0.0)],"derivedFrom":[subQ1,subQ0]});Q2=makeQuery(id+"F30.imprint","IMPRINT",FACE,{"disambiguationData":[TD([[makeQuery(id+"F30.imprint","IMPRINT",EDGE,{"disambiguationData":[TD([[subQ2,-1.0]])],"derivedFrom":subQ1}),1.0]])]});}
            var Q3;
            {var subQ0=sQuery(id+"F30.wireOp",EDGE,"E66.0");var subQ1=sQuery(id+"F30.wireOp",EDGE,"E64.top");var subQ2=makeQuery(id+"F30.imprint","INTERSECT",VERTEX,{"disambiguationData":[OD(0.0)],"derivedFrom":[subQ1,subQ0]});Q3=makeQuery(id+"F30.imprint","IMPRINT",FACE,{"disambiguationData":[TD([[makeQuery(id+"F30.imprint","IMPRINT",EDGE,{"disambiguationData":[TD([[subQ2,-1.0]])],"derivedFrom":subQ1}),1.0]])]});}
            var Q4;
            {var subQ0=sQuery(id+"F30.wireOp",EDGE,"E66.1");var subQ1=sQuery(id+"F30.wireOp",EDGE,"E65.bottom");var subQ2=makeQuery(id+"F30.imprint","INTERSECT",VERTEX,{"disambiguationData":[OD(0.0)],"derivedFrom":[subQ1,subQ0]});Q4=makeQuery(id+"F30.imprint","IMPRINT",FACE,{"disambiguationData":[TD([[makeQuery(id+"F30.imprint","IMPRINT",EDGE,{"disambiguationData":[TD([[subQ2,-1.0]])],"derivedFrom":subQ1}),-1.0]])]});}
            var Q5;
            {var subQ0=sQuery(id+"F30.wireOp",EDGE,"E66.1");var subQ1=sQuery(id+"F30.wireOp",EDGE,"E65.left");var subQ2=makeQuery(id+"F30.imprint","INTERSECT",VERTEX,{"disambiguationData":[OD(0.0)],"derivedFrom":[subQ1,subQ0]});Q5=makeQuery(id+"F30.imprint","IMPRINT",FACE,{"disambiguationData":[TD([[makeQuery(id+"F30.imprint","IMPRINT",EDGE,{"disambiguationData":[TD([[subQ2,-1.0]])],"derivedFrom":subQ1}),1.0]])]});}
            var Q6;
            {var subQ0=sQuery(id+"F30.wireOp",EDGE,"E66.1");var subQ1=sQuery(id+"F30.wireOp",EDGE,"E65.right");var subQ2=makeQuery(id+"F30.imprint","INTERSECT",VERTEX,{"disambiguationData":[OD(0.0)],"derivedFrom":[subQ1,subQ0]});Q6=makeQuery(id+"F30.imprint","IMPRINT",FACE,{"disambiguationData":[TD([[makeQuery(id+"F30.imprint","IMPRINT",EDGE,{"disambiguationData":[TD([[subQ2,-1.0]])],"derivedFrom":subQ1}),-1.0]])]});}
            var Q7;
            {var subQ0=sQuery(id+"F30.wireOp",EDGE,"E66.1");var subQ1=sQuery(id+"F30.wireOp",EDGE,"E65.top");var subQ2=makeQuery(id+"F30.imprint","INTERSECT",VERTEX,{"disambiguationData":[OD(0.0)],"derivedFrom":[subQ1,subQ0]});Q7=makeQuery(id+"F30.imprint","IMPRINT",FACE,{"disambiguationData":[TD([[makeQuery(id+"F30.imprint","IMPRINT",EDGE,{"disambiguationData":[TD([[subQ2,-1.0]])],"derivedFrom":subQ1}),1.0]])]});}
            extrude(context, id + "F31", {"entities" : qUnion([Q0, Q1, Q2, Q3, Q4, Q5, Q6, Q7]), "operationType" : NewBodyOperationType.ADD, "depth" : 3.86 * mm, "offsetDistance" : 25.4 * mm});
        }
        {
            var Q0;
            Q0=makeQuery(id+"F27.boolean.opBoolean","COPY",FACE,{"derivedFrom":makeQuery(id+"F27.opExtrude","CAP_FACE",FACE,{"disambiguationData":[OSD([sQuery(id+"F26.wireOp",EDGE,"E59.0")])],"isStart":false})});
            var sketch = newSketch(context, id + "F32", { "sketchPlane" : qUnion([Q0])});
            skLineSegment(sketch, "E67.0.0", {"start": v(-1.17, 9.14) * mm, "end": v(-3.48, 9.14) * mm});
            skArc(sketch, "E67.0.1", {"start": v(-3.48, 9.14) * mm, "mid": v(-2.33, 9.42) * mm, "end": v(-1.17, 9.14) * mm});
            skLineSegment(sketch, "E67.1.0", {"start": v(-4.58, 8.05) * mm, "end": v(-4.58, 5.74) * mm});
            skArc(sketch, "E67.1.1", {"start": v(-4.58, 5.74) * mm, "mid": v(-4.86, 6.9) * mm, "end": v(-4.58, 8.05) * mm});
            skLineSegment(sketch, "E67.2.0", {"start": v(-3.48, 4.65) * mm, "end": v(-1.17, 4.65) * mm});
            skArc(sketch, "E67.2.1", {"start": v(-1.17, 4.65) * mm, "mid": v(-2.33, 4.37) * mm, "end": v(-3.48, 4.65) * mm});
            skLineSegment(sketch, "E67.3.0", {"start": v(-0.08, 5.74) * mm, "end": v(-0.08, 8.05) * mm});
            skArc(sketch, "E67.3.1", {"start": v(-0.08, 8.05) * mm, "mid": v(0.2, 6.9) * mm, "end": v(-0.08, 5.74) * mm});
            skLineSegment(sketch, "E67.4.0", {"start": v(12.7, 9.14) * mm, "end": v(10.4, 9.14) * mm});
            skArc(sketch, "E67.4.1", {"start": v(10.4, 9.14) * mm, "mid": v(11.55, 9.42) * mm, "end": v(12.7, 9.14) * mm});
            skArc(sketch, "E67.5.0", {"start": v(9.3, 5.74) * mm, "mid": v(9.03, 6.9) * mm, "end": v(9.3, 8.05) * mm});
            skLineSegment(sketch, "E67.5.1", {"start": v(9.3, 8.05) * mm, "end": v(9.3, 5.74) * mm});
            skArc(sketch, "E67.6.0", {"start": v(12.7, 4.65) * mm, "mid": v(11.55, 4.37) * mm, "end": v(10.4, 4.65) * mm});
            skLineSegment(sketch, "E67.6.1", {"start": v(10.4, 4.65) * mm, "end": v(12.7, 4.65) * mm});
            skLineSegment(sketch, "E67.7.0", {"start": v(13.8, 5.74) * mm, "end": v(13.8, 8.05) * mm});
            skArc(sketch, "E67.7.1", {"start": v(13.8, 8.05) * mm, "mid": v(14.08, 6.9) * mm, "end": v(13.8, 5.74) * mm});
            skSolve(sketch);
        }
        {
            var Q0;
            Q0=qSketchRegion(id+"F32",true);
            extrude(context, id + "F33", {"entities" : qUnion([Q0]), "operationType" : NewBodyOperationType.ADD, "depth" : 3.86 * mm, "offsetDistance" : 25.4 * mm});
        }
        {
            var Q0;
            Q0=makeQuery(id+"F9.boolean.opBoolean","MERGE",FACE,{"derivedFrom":[makeQuery(id+"F1.opExtrude","CAP_FACE",FACE,{"disambiguationData":[OSD([sQuery(id+"F0.wireOp",EDGE,"E0.bottom"),sQuery(id+"F0.wireOp",EDGE,"E0.top"),sQuery(id+"F0.wireOp",EDGE,"E0.left"),sQuery(id+"F0.wireOp",EDGE,"E0.right")])],"isStart":false}),makeQuery(id+"F9.opExtrude","CAP_FACE",FACE,{"disambiguationData":[OSD([sQuery(id+"F8.wireOp",EDGE,"E8")])],"isStart":false})]});
            var sketch = newSketch(context, id + "F34", { "sketchPlane" : qUnion([Q0])});
            skLineSegment(sketch, "E68", {"start": v(-12.61, -18.5) * mm, "end": v(15.28, 9.27) * mm, "construction": true});
            skLineSegment(sketch, "E69", {"start": v(-5.58, -14.76) * mm, "end": v(-8.75, -11.58) * mm});
            skLineSegment(sketch, "E70", {"start": v(-8.75, -11.58) * mm, "end": v(-5.57, -8.4) * mm});
            skLineSegment(sketch, "E71", {"start": v(-5.57, -8.4) * mm, "end": v(-2.4, -11.6) * mm});
            skLineSegment(sketch, "E72", {"start": v(-2.4, -11.6) * mm, "end": v(-5.58, -14.76) * mm});
            skLineSegment(sketch, "E73", {"start": v(-7.16, -10) * mm, "end": v(-3.99, -13.18) * mm});
            skPoint(sketch, "E74", {"position": v(-5.57, -11.58) * mm});
            skLineSegment(sketch, "E75.1.0", {"start": v(11.49, -11.53) * mm, "end": v(8.3, -14.7) * mm});
            skLineSegment(sketch, "E75.1.1", {"start": v(8.31, -8.34) * mm, "end": v(11.49, -11.53) * mm});
            skLineSegment(sketch, "E75.1.2", {"start": v(5.13, -11.51) * mm, "end": v(8.31, -8.34) * mm});
            skLineSegment(sketch, "E75.1.3", {"start": v(8.3, -14.7) * mm, "end": v(5.13, -11.51) * mm});
            skLineSegment(sketch, "E75.2.0", {"start": v(8.25, 5.54) * mm, "end": v(11.42, 2.35) * mm});
            skLineSegment(sketch, "E75.2.1", {"start": v(5.06, 2.37) * mm, "end": v(8.25, 5.54) * mm});
            skLineSegment(sketch, "E75.2.2", {"start": v(8.24, -0.82) * mm, "end": v(5.06, 2.37) * mm});
            skLineSegment(sketch, "E75.2.3", {"start": v(11.42, 2.35) * mm, "end": v(8.24, -0.82) * mm});
            skLineSegment(sketch, "E75.3.0", {"start": v(-8.82, 2.3) * mm, "end": v(-5.63, 5.48) * mm});
            skLineSegment(sketch, "E75.3.1", {"start": v(-5.65, -0.88) * mm, "end": v(-8.82, 2.3) * mm});
            skLineSegment(sketch, "E75.3.2", {"start": v(-2.46, 2.29) * mm, "end": v(-5.65, -0.88) * mm});
            skLineSegment(sketch, "E75.3.3", {"start": v(-5.63, 5.48) * mm, "end": v(-2.46, 2.29) * mm});
            skPoint(sketch, "E75.center", {"position": v(1.33, -4.61) * mm});
            skCircle(sketch, "E76.0", {"center": v(-5.57, -11.58) * mm, "radius": 2.53 * mm});
            skCircle(sketch, "E77.1.0", {"center": v(8.3, -11.52) * mm, "radius": 2.53 * mm});
            skCircle(sketch, "E77.2.0", {"center": v(8.24, 2.36) * mm, "radius": 2.53 * mm});
            skCircle(sketch, "E77.3.0", {"center": v(-5.64, 2.3) * mm, "radius": 2.53 * mm});
            skSolve(sketch);
        }
        {
            var Q0;
            {var subQ0=sQuery(id+"F34.wireOp",EDGE,"E77.1.0");var subQ1=sQuery(id+"F34.wireOp",EDGE,"E75.1.0");var subQ2=makeQuery(id+"F34.imprint","INTERSECT",VERTEX,{"disambiguationData":[OD(0.0)],"derivedFrom":[subQ1,subQ0]});Q0=makeQuery(id+"F34.imprint","IMPRINT",FACE,{"disambiguationData":[TD([[makeQuery(id+"F34.imprint","IMPRINT",EDGE,{"disambiguationData":[TD([[subQ2,-1.0]])],"derivedFrom":subQ1}),1.0]])]});}
            var Q1;
            {var subQ0=sQuery(id+"F34.wireOp",EDGE,"E77.1.0");var subQ1=sQuery(id+"F34.wireOp",EDGE,"E75.1.3");var subQ2=makeQuery(id+"F34.imprint","INTERSECT",VERTEX,{"disambiguationData":[OD(0.0)],"derivedFrom":[subQ1,subQ0]});Q1=makeQuery(id+"F34.imprint","IMPRINT",FACE,{"disambiguationData":[TD([[makeQuery(id+"F34.imprint","IMPRINT",EDGE,{"disambiguationData":[TD([[subQ2,-1.0]])],"derivedFrom":subQ1}),1.0]])]});}
            var Q2;
            {var subQ0=sQuery(id+"F34.wireOp",EDGE,"E77.1.0");var subQ1=sQuery(id+"F34.wireOp",EDGE,"E75.1.1");var subQ2=makeQuery(id+"F34.imprint","INTERSECT",VERTEX,{"disambiguationData":[OD(0.0)],"derivedFrom":[subQ1,subQ0]});Q2=makeQuery(id+"F34.imprint","IMPRINT",FACE,{"disambiguationData":[TD([[makeQuery(id+"F34.imprint","IMPRINT",EDGE,{"disambiguationData":[TD([[subQ2,-1.0]])],"derivedFrom":subQ1}),1.0]])]});}
            var Q3;
            {var subQ0=sQuery(id+"F34.wireOp",EDGE,"E77.1.0");var subQ1=sQuery(id+"F34.wireOp",EDGE,"E75.1.2");var subQ2=makeQuery(id+"F34.imprint","INTERSECT",VERTEX,{"disambiguationData":[OD(0.0)],"derivedFrom":[subQ1,subQ0]});Q3=makeQuery(id+"F34.imprint","IMPRINT",FACE,{"disambiguationData":[TD([[makeQuery(id+"F34.imprint","IMPRINT",EDGE,{"disambiguationData":[TD([[subQ2,-1.0]])],"derivedFrom":subQ1}),1.0]])]});}
            var Q4;
            {var subQ0=sQuery(id+"F34.wireOp",EDGE,"E70");var subQ1=makeQuery(id+"F34.imprint","INTERSECT",VERTEX,{"derivedFrom":[subQ0,sQuery(id+"F34.wireOp",EDGE,"E73")]});Q4=makeQuery(id+"F34.imprint","IMPRINT",FACE,{"disambiguationData":[TD([[makeQuery(id+"F34.imprint","IMPRINT",EDGE,{"disambiguationData":[TD([[subQ1,1.0]])],"derivedFrom":subQ0}),1.0]])]});}
            var Q5;
            {var subQ0=sQuery(id+"F34.wireOp",EDGE,"E76.0");var subQ1=sQuery(id+"F34.wireOp",EDGE,"E71");var subQ2=makeQuery(id+"F34.imprint","INTERSECT",VERTEX,{"disambiguationData":[OD(0.0)],"derivedFrom":[subQ1,subQ0]});Q5=makeQuery(id+"F34.imprint","IMPRINT",FACE,{"disambiguationData":[TD([[makeQuery(id+"F34.imprint","IMPRINT",EDGE,{"disambiguationData":[TD([[subQ2,-1.0]])],"derivedFrom":subQ1}),1.0]])]});}
            var Q6;
            {var subQ0=sQuery(id+"F34.wireOp",EDGE,"E72");var subQ1=makeQuery(id+"F34.imprint","INTERSECT",VERTEX,{"derivedFrom":[subQ0,sQuery(id+"F34.wireOp",EDGE,"E73")]});Q6=makeQuery(id+"F34.imprint","IMPRINT",FACE,{"disambiguationData":[TD([[makeQuery(id+"F34.imprint","IMPRINT",EDGE,{"disambiguationData":[TD([[subQ1,1.0]])],"derivedFrom":subQ0}),1.0]])]});}
            var Q7;
            {var subQ0=sQuery(id+"F34.wireOp",EDGE,"E76.0");var subQ1=sQuery(id+"F34.wireOp",EDGE,"E69");var subQ2=makeQuery(id+"F34.imprint","INTERSECT",VERTEX,{"disambiguationData":[OD(0.0)],"derivedFrom":[subQ1,subQ0]});Q7=makeQuery(id+"F34.imprint","IMPRINT",FACE,{"disambiguationData":[TD([[makeQuery(id+"F34.imprint","IMPRINT",EDGE,{"disambiguationData":[TD([[subQ2,-1.0]])],"derivedFrom":subQ1}),1.0]])]});}
            var Q8;
            {var subQ0=sQuery(id+"F34.wireOp",EDGE,"E77.3.0");var subQ1=sQuery(id+"F34.wireOp",EDGE,"E75.3.0");var subQ2=makeQuery(id+"F34.imprint","INTERSECT",VERTEX,{"disambiguationData":[OD(0.0)],"derivedFrom":[subQ1,subQ0]});Q8=makeQuery(id+"F34.imprint","IMPRINT",FACE,{"disambiguationData":[TD([[makeQuery(id+"F34.imprint","IMPRINT",EDGE,{"disambiguationData":[TD([[subQ2,-1.0]])],"derivedFrom":subQ1}),1.0]])]});}
            var Q9;
            {var subQ0=sQuery(id+"F34.wireOp",EDGE,"E77.3.0");var subQ1=sQuery(id+"F34.wireOp",EDGE,"E75.3.3");var subQ2=makeQuery(id+"F34.imprint","INTERSECT",VERTEX,{"disambiguationData":[OD(0.0)],"derivedFrom":[subQ1,subQ0]});Q9=makeQuery(id+"F34.imprint","IMPRINT",FACE,{"disambiguationData":[TD([[makeQuery(id+"F34.imprint","IMPRINT",EDGE,{"disambiguationData":[TD([[subQ2,-1.0]])],"derivedFrom":subQ1}),1.0]])]});}
            var Q10;
            {var subQ0=sQuery(id+"F34.wireOp",EDGE,"E77.3.0");var subQ1=sQuery(id+"F34.wireOp",EDGE,"E75.3.1");var subQ2=makeQuery(id+"F34.imprint","INTERSECT",VERTEX,{"disambiguationData":[OD(0.0)],"derivedFrom":[subQ1,subQ0]});Q10=makeQuery(id+"F34.imprint","IMPRINT",FACE,{"disambiguationData":[TD([[makeQuery(id+"F34.imprint","IMPRINT",EDGE,{"disambiguationData":[TD([[subQ2,-1.0]])],"derivedFrom":subQ1}),1.0]])]});}
            var Q11;
            {var subQ0=sQuery(id+"F34.wireOp",EDGE,"E77.3.0");var subQ1=sQuery(id+"F34.wireOp",EDGE,"E75.3.2");var subQ2=makeQuery(id+"F34.imprint","INTERSECT",VERTEX,{"disambiguationData":[OD(0.0)],"derivedFrom":[subQ1,subQ0]});Q11=makeQuery(id+"F34.imprint","IMPRINT",FACE,{"disambiguationData":[TD([[makeQuery(id+"F34.imprint","IMPRINT",EDGE,{"disambiguationData":[TD([[subQ2,-1.0]])],"derivedFrom":subQ1}),1.0]])]});}
            var Q12;
            {var subQ0=sQuery(id+"F34.wireOp",EDGE,"E77.2.0");var subQ1=sQuery(id+"F34.wireOp",EDGE,"E75.2.0");var subQ2=makeQuery(id+"F34.imprint","INTERSECT",VERTEX,{"disambiguationData":[OD(0.0)],"derivedFrom":[subQ1,subQ0]});Q12=makeQuery(id+"F34.imprint","IMPRINT",FACE,{"disambiguationData":[TD([[makeQuery(id+"F34.imprint","IMPRINT",EDGE,{"disambiguationData":[TD([[subQ2,-1.0]])],"derivedFrom":subQ1}),1.0]])]});}
            var Q13;
            {var subQ0=sQuery(id+"F34.wireOp",EDGE,"E77.2.0");var subQ1=sQuery(id+"F34.wireOp",EDGE,"E75.2.1");var subQ2=makeQuery(id+"F34.imprint","INTERSECT",VERTEX,{"disambiguationData":[OD(0.0)],"derivedFrom":[subQ1,subQ0]});Q13=makeQuery(id+"F34.imprint","IMPRINT",FACE,{"disambiguationData":[TD([[makeQuery(id+"F34.imprint","IMPRINT",EDGE,{"disambiguationData":[TD([[subQ2,-1.0]])],"derivedFrom":subQ1}),1.0]])]});}
            var Q14;
            {var subQ0=sQuery(id+"F34.wireOp",EDGE,"E77.2.0");var subQ1=sQuery(id+"F34.wireOp",EDGE,"E75.2.2");var subQ2=makeQuery(id+"F34.imprint","INTERSECT",VERTEX,{"disambiguationData":[OD(0.0)],"derivedFrom":[subQ1,subQ0]});Q14=makeQuery(id+"F34.imprint","IMPRINT",FACE,{"disambiguationData":[TD([[makeQuery(id+"F34.imprint","IMPRINT",EDGE,{"disambiguationData":[TD([[subQ2,-1.0]])],"derivedFrom":subQ1}),1.0]])]});}
            var Q15;
            {var subQ0=sQuery(id+"F34.wireOp",EDGE,"E77.2.0");var subQ1=sQuery(id+"F34.wireOp",EDGE,"E75.2.3");var subQ2=makeQuery(id+"F34.imprint","INTERSECT",VERTEX,{"disambiguationData":[OD(0.0)],"derivedFrom":[subQ1,subQ0]});Q15=makeQuery(id+"F34.imprint","IMPRINT",FACE,{"disambiguationData":[TD([[makeQuery(id+"F34.imprint","IMPRINT",EDGE,{"disambiguationData":[TD([[subQ2,-1.0]])],"derivedFrom":subQ1}),1.0]])]});}
            extrude(context, id + "F35", {"entities" : qUnion([Q0, Q1, Q2, Q3, Q4, Q5, Q6, Q7, Q8, Q9, Q10, Q11, Q12, Q13, Q14, Q15]), "operationType" : NewBodyOperationType.ADD, "oppositeDirection" : true, "depth" : 13.8 * mm, "offsetDistance" : 25.4 * mm});
        }
        {
            var Q0;
            {var subQ0=sQuery(id+"F34.wireOp",EDGE,"E77.3.0");var subQ1=sQuery(id+"F34.wireOp",EDGE,"E77.2.0");var subQ2=sQuery(id+"F34.wireOp",EDGE,"E77.1.0");var subQ3=sQuery(id+"F34.wireOp",EDGE,"E76.0");Q0=makeQuery(id+"F35.boolean.opBoolean","MERGE",FACE,{"derivedFrom":[makeQuery(id+"F9.boolean.opBoolean","MERGE",FACE,{"derivedFrom":[makeQuery(id+"F1.opExtrude","CAP_FACE",FACE,{"disambiguationData":[OSD([sQuery(id+"F0.wireOp",EDGE,"E0.bottom"),sQuery(id+"F0.wireOp",EDGE,"E0.top"),sQuery(id+"F0.wireOp",EDGE,"E0.left"),sQuery(id+"F0.wireOp",EDGE,"E0.right")])],"isStart":false}),makeQuery(id+"F9.opExtrude","CAP_FACE",FACE,{"disambiguationData":[OSD([sQuery(id+"F8.wireOp",EDGE,"E8")])],"isStart":false})]}),makeQuery(id+"F35.opExtrude","CAP_FACE",FACE,{"disambiguationData":[OSD([sQuery(id+"F34.wireOp",EDGE,"E69"),subQ3])],"isStart":true}),makeQuery(id+"F35.opExtrude","CAP_FACE",FACE,{"disambiguationData":[OSD([sQuery(id+"F34.wireOp",EDGE,"E70"),subQ3])],"isStart":true}),makeQuery(id+"F35.opExtrude","CAP_FACE",FACE,{"disambiguationData":[OSD([sQuery(id+"F34.wireOp",EDGE,"E71"),subQ3])],"isStart":true}),makeQuery(id+"F35.opExtrude","CAP_FACE",FACE,{"disambiguationData":[OSD([sQuery(id+"F34.wireOp",EDGE,"E72"),subQ3])],"isStart":true}),makeQuery(id+"F35.opExtrude","CAP_FACE",FACE,{"disambiguationData":[OSD([sQuery(id+"F34.wireOp",EDGE,"E75.1.0"),subQ2])],"isStart":true}),makeQuery(id+"F35.opExtrude","CAP_FACE",FACE,{"disambiguationData":[OSD([sQuery(id+"F34.wireOp",EDGE,"E75.1.1"),subQ2])],"isStart":true}),makeQuery(id+"F35.opExtrude","CAP_FACE",FACE,{"disambiguationData":[OSD([sQuery(id+"F34.wireOp",EDGE,"E75.1.2"),subQ2])],"isStart":true}),makeQuery(id+"F35.opExtrude","CAP_FACE",FACE,{"disambiguationData":[OSD([sQuery(id+"F34.wireOp",EDGE,"E75.1.3"),subQ2])],"isStart":true}),makeQuery(id+"F35.opExtrude","CAP_FACE",FACE,{"disambiguationData":[OSD([sQuery(id+"F34.wireOp",EDGE,"E75.2.0"),subQ1])],"isStart":true}),makeQuery(id+"F35.opExtrude","CAP_FACE",FACE,{"disambiguationData":[OSD([sQuery(id+"F34.wireOp",EDGE,"E75.2.1"),subQ1])],"isStart":true}),makeQuery(id+"F35.opExtrude","CAP_FACE",FACE,{"disambiguationData":[OSD([sQuery(id+"F34.wireOp",EDGE,"E75.2.2"),subQ1])],"isStart":true}),makeQuery(id+"F35.opExtrude","CAP_FACE",FACE,{"disambiguationData":[OSD([sQuery(id+"F34.wireOp",EDGE,"E75.2.3"),subQ1])],"isStart":true}),makeQuery(id+"F35.opExtrude","CAP_FACE",FACE,{"disambiguationData":[OSD([sQuery(id+"F34.wireOp",EDGE,"E75.3.0"),subQ0])],"isStart":true}),makeQuery(id+"F35.opExtrude","CAP_FACE",FACE,{"disambiguationData":[OSD([sQuery(id+"F34.wireOp",EDGE,"E75.3.1"),subQ0])],"isStart":true}),makeQuery(id+"F35.opExtrude","CAP_FACE",FACE,{"disambiguationData":[OSD([sQuery(id+"F34.wireOp",EDGE,"E75.3.2"),subQ0])],"isStart":true}),makeQuery(id+"F35.opExtrude","CAP_FACE",FACE,{"disambiguationData":[OSD([sQuery(id+"F34.wireOp",EDGE,"E75.3.3"),subQ0])],"isStart":true})]});}
            var sketch = newSketch(context, id + "F36", { "sketchPlane" : qUnion([Q0])});
            skCircle(sketch, "E78", {"center": v(8.24, 2.36) * mm, "radius": 2.53 * mm});
            skLineSegment(sketch, "E79.0", {"start": v(10.65, 1.58) * mm, "end": v(9.01, -0.05) * mm});
            skLineSegment(sketch, "E79.1", {"start": v(9.02, 4.76) * mm, "end": v(10.65, 3.13) * mm});
            skLineSegment(sketch, "E79.2", {"start": v(5.84, 3.14) * mm, "end": v(7.48, 4.77) * mm});
            skLineSegment(sketch, "E79.3", {"start": v(7.46, -0.04) * mm, "end": v(5.84, 1.6) * mm});
            skCircle(sketch, "E80.1.0", {"center": v(-5.64, 2.3) * mm, "radius": 2.53 * mm});
            skLineSegment(sketch, "E80.1.1", {"start": v(-4.86, 4.7) * mm, "end": v(-3.23, 3.06) * mm});
            skLineSegment(sketch, "E80.1.2", {"start": v(-8.04, 3.07) * mm, "end": v(-6.4, 4.7) * mm});
            skLineSegment(sketch, "E80.1.3", {"start": v(-6.42, -0.1) * mm, "end": v(-8.05, 1.53) * mm});
            skLineSegment(sketch, "E80.1.4", {"start": v(-3.23, 1.52) * mm, "end": v(-4.87, -0.11) * mm});
            skCircle(sketch, "E80.2.0", {"center": v(-5.57, -11.58) * mm, "radius": 2.53 * mm});
            skLineSegment(sketch, "E80.2.1", {"start": v(-7.98, -10.8) * mm, "end": v(-6.34, -9.18) * mm});
            skLineSegment(sketch, "E80.2.2", {"start": v(-6.35, -13.99) * mm, "end": v(-7.98, -12.35) * mm});
            skLineSegment(sketch, "E80.2.3", {"start": v(-3.17, -12.36) * mm, "end": v(-4.8, -14) * mm});
            skLineSegment(sketch, "E80.2.4", {"start": v(-4.8, -9.18) * mm, "end": v(-3.17, -10.82) * mm});
            skCircle(sketch, "E80.3.0", {"center": v(8.3, -11.52) * mm, "radius": 2.53 * mm});
            skLineSegment(sketch, "E80.3.1", {"start": v(7.53, -13.93) * mm, "end": v(5.9, -12.29) * mm});
            skLineSegment(sketch, "E80.3.2", {"start": v(10.71, -12.3) * mm, "end": v(9.07, -13.93) * mm});
            skLineSegment(sketch, "E80.3.3", {"start": v(9.08, -9.12) * mm, "end": v(10.71, -10.75) * mm});
            skLineSegment(sketch, "E80.3.4", {"start": v(5.9, -10.74) * mm, "end": v(7.54, -9.11) * mm});
            skPoint(sketch, "E80.center", {"position": v(1.33, -4.61) * mm});
            skSolve(sketch);
        }
        {
            var Q0;
            {var subQ0=sQuery(id+"F36.wireOp",EDGE,"E79.1");var subQ1=sQuery(id+"F36.wireOp",EDGE,"E78");var subQ2=makeQuery(id+"F36.imprint","INTERSECT",VERTEX,{"disambiguationData":[OD(0.0)],"derivedFrom":[subQ1,subQ0]});Q0=makeQuery(id+"F36.imprint","IMPRINT",FACE,{"disambiguationData":[TD([[makeQuery(id+"F36.imprint","IMPRINT",EDGE,{"disambiguationData":[TD([[subQ2,1.0]])],"derivedFrom":subQ1}),1.0]])]});}
            var Q1;
            {var subQ0=sQuery(id+"F36.wireOp",EDGE,"E79.2");var subQ1=sQuery(id+"F36.wireOp",EDGE,"E78");var subQ2=makeQuery(id+"F36.imprint","INTERSECT",VERTEX,{"disambiguationData":[OD(0.0)],"derivedFrom":[subQ1,subQ0]});Q1=makeQuery(id+"F36.imprint","IMPRINT",FACE,{"disambiguationData":[TD([[makeQuery(id+"F36.imprint","IMPRINT",EDGE,{"disambiguationData":[TD([[subQ2,-1.0]])],"derivedFrom":subQ1}),1.0]])]});}
            var Q2;
            {var subQ0=sQuery(id+"F36.wireOp",EDGE,"E79.3");var subQ1=sQuery(id+"F36.wireOp",EDGE,"E78");var subQ2=makeQuery(id+"F36.imprint","INTERSECT",VERTEX,{"disambiguationData":[OD(0.0)],"derivedFrom":[subQ1,subQ0]});Q2=makeQuery(id+"F36.imprint","IMPRINT",FACE,{"disambiguationData":[TD([[makeQuery(id+"F36.imprint","IMPRINT",EDGE,{"disambiguationData":[TD([[subQ2,-1.0]])],"derivedFrom":subQ1}),1.0]])]});}
            var Q3;
            {var subQ0=sQuery(id+"F36.wireOp",EDGE,"E79.0");var subQ1=sQuery(id+"F36.wireOp",EDGE,"E78");var subQ2=makeQuery(id+"F36.imprint","INTERSECT",VERTEX,{"disambiguationData":[OD(0.0)],"derivedFrom":[subQ1,subQ0]});Q3=makeQuery(id+"F36.imprint","IMPRINT",FACE,{"disambiguationData":[TD([[makeQuery(id+"F36.imprint","IMPRINT",EDGE,{"disambiguationData":[TD([[subQ2,-1.0]])],"derivedFrom":subQ1}),1.0]])]});}
            var Q4;
            {var subQ0=sQuery(id+"F36.wireOp",EDGE,"E80.1.2");var subQ1=sQuery(id+"F36.wireOp",EDGE,"E80.1.0");var subQ2=makeQuery(id+"F36.imprint","INTERSECT",VERTEX,{"disambiguationData":[OD(0.0)],"derivedFrom":[subQ1,subQ0]});Q4=makeQuery(id+"F36.imprint","IMPRINT",FACE,{"disambiguationData":[TD([[makeQuery(id+"F36.imprint","IMPRINT",EDGE,{"disambiguationData":[TD([[subQ2,1.0]])],"derivedFrom":subQ1}),1.0]])]});}
            var Q5;
            {var subQ0=sQuery(id+"F36.wireOp",EDGE,"E80.1.3");var subQ1=sQuery(id+"F36.wireOp",EDGE,"E80.1.0");var subQ2=makeQuery(id+"F36.imprint","INTERSECT",VERTEX,{"disambiguationData":[OD(0.0)],"derivedFrom":[subQ1,subQ0]});Q5=makeQuery(id+"F36.imprint","IMPRINT",FACE,{"disambiguationData":[TD([[makeQuery(id+"F36.imprint","IMPRINT",EDGE,{"disambiguationData":[TD([[subQ2,-1.0]])],"derivedFrom":subQ1}),1.0]])]});}
            var Q6;
            {var subQ0=sQuery(id+"F36.wireOp",EDGE,"E80.1.4");var subQ1=sQuery(id+"F36.wireOp",EDGE,"E80.1.0");var subQ2=makeQuery(id+"F36.imprint","INTERSECT",VERTEX,{"disambiguationData":[OD(0.0)],"derivedFrom":[subQ1,subQ0]});Q6=makeQuery(id+"F36.imprint","IMPRINT",FACE,{"disambiguationData":[TD([[makeQuery(id+"F36.imprint","IMPRINT",EDGE,{"disambiguationData":[TD([[subQ2,-1.0]])],"derivedFrom":subQ1}),1.0]])]});}
            var Q7;
            {var subQ0=sQuery(id+"F36.wireOp",EDGE,"E80.1.1");var subQ1=sQuery(id+"F36.wireOp",EDGE,"E80.1.0");var subQ2=makeQuery(id+"F36.imprint","INTERSECT",VERTEX,{"disambiguationData":[OD(0.0)],"derivedFrom":[subQ1,subQ0]});Q7=makeQuery(id+"F36.imprint","IMPRINT",FACE,{"disambiguationData":[TD([[makeQuery(id+"F36.imprint","IMPRINT",EDGE,{"disambiguationData":[TD([[subQ2,-1.0]])],"derivedFrom":subQ1}),1.0]])]});}
            var Q8;
            {var subQ0=sQuery(id+"F36.wireOp",EDGE,"E80.2.2");var subQ1=sQuery(id+"F36.wireOp",EDGE,"E80.2.0");var subQ2=makeQuery(id+"F36.imprint","INTERSECT",VERTEX,{"disambiguationData":[OD(0.0)],"derivedFrom":[subQ1,subQ0]});Q8=makeQuery(id+"F36.imprint","IMPRINT",FACE,{"disambiguationData":[TD([[makeQuery(id+"F36.imprint","IMPRINT",EDGE,{"disambiguationData":[TD([[subQ2,1.0]])],"derivedFrom":subQ1}),1.0]])]});}
            var Q9;
            {var subQ0=sQuery(id+"F36.wireOp",EDGE,"E80.2.3");var subQ1=sQuery(id+"F36.wireOp",EDGE,"E80.2.0");var subQ2=makeQuery(id+"F36.imprint","INTERSECT",VERTEX,{"disambiguationData":[OD(0.0)],"derivedFrom":[subQ1,subQ0]});Q9=makeQuery(id+"F36.imprint","IMPRINT",FACE,{"disambiguationData":[TD([[makeQuery(id+"F36.imprint","IMPRINT",EDGE,{"disambiguationData":[TD([[subQ2,-1.0]])],"derivedFrom":subQ1}),1.0]])]});}
            var Q10;
            {var subQ0=sQuery(id+"F36.wireOp",EDGE,"E80.2.4");var subQ1=sQuery(id+"F36.wireOp",EDGE,"E80.2.0");var subQ2=makeQuery(id+"F36.imprint","INTERSECT",VERTEX,{"disambiguationData":[OD(0.0)],"derivedFrom":[subQ1,subQ0]});Q10=makeQuery(id+"F36.imprint","IMPRINT",FACE,{"disambiguationData":[TD([[makeQuery(id+"F36.imprint","IMPRINT",EDGE,{"disambiguationData":[TD([[subQ2,-1.0]])],"derivedFrom":subQ1}),1.0]])]});}
            var Q11;
            {var subQ0=sQuery(id+"F36.wireOp",EDGE,"E80.2.1");var subQ1=sQuery(id+"F36.wireOp",EDGE,"E80.2.0");var subQ2=makeQuery(id+"F36.imprint","INTERSECT",VERTEX,{"disambiguationData":[OD(0.0)],"derivedFrom":[subQ1,subQ0]});Q11=makeQuery(id+"F36.imprint","IMPRINT",FACE,{"disambiguationData":[TD([[makeQuery(id+"F36.imprint","IMPRINT",EDGE,{"disambiguationData":[TD([[subQ2,-1.0]])],"derivedFrom":subQ1}),1.0]])]});}
            var Q12;
            {var subQ0=sQuery(id+"F36.wireOp",EDGE,"E80.3.2");var subQ1=sQuery(id+"F36.wireOp",EDGE,"E80.3.0");var subQ2=makeQuery(id+"F36.imprint","INTERSECT",VERTEX,{"disambiguationData":[OD(0.0)],"derivedFrom":[subQ1,subQ0]});Q12=makeQuery(id+"F36.imprint","IMPRINT",FACE,{"disambiguationData":[TD([[makeQuery(id+"F36.imprint","IMPRINT",EDGE,{"disambiguationData":[TD([[subQ2,1.0]])],"derivedFrom":subQ1}),1.0]])]});}
            var Q13;
            {var subQ0=sQuery(id+"F36.wireOp",EDGE,"E80.3.3");var subQ1=sQuery(id+"F36.wireOp",EDGE,"E80.3.0");var subQ2=makeQuery(id+"F36.imprint","INTERSECT",VERTEX,{"disambiguationData":[OD(0.0)],"derivedFrom":[subQ1,subQ0]});Q13=makeQuery(id+"F36.imprint","IMPRINT",FACE,{"disambiguationData":[TD([[makeQuery(id+"F36.imprint","IMPRINT",EDGE,{"disambiguationData":[TD([[subQ2,-1.0]])],"derivedFrom":subQ1}),1.0]])]});}
            var Q14;
            {var subQ0=sQuery(id+"F36.wireOp",EDGE,"E80.3.4");var subQ1=sQuery(id+"F36.wireOp",EDGE,"E80.3.0");var subQ2=makeQuery(id+"F36.imprint","INTERSECT",VERTEX,{"disambiguationData":[OD(0.0)],"derivedFrom":[subQ1,subQ0]});Q14=makeQuery(id+"F36.imprint","IMPRINT",FACE,{"disambiguationData":[TD([[makeQuery(id+"F36.imprint","IMPRINT",EDGE,{"disambiguationData":[TD([[subQ2,-1.0]])],"derivedFrom":subQ1}),1.0]])]});}
            var Q15;
            {var subQ0=sQuery(id+"F36.wireOp",EDGE,"E80.3.1");var subQ1=sQuery(id+"F36.wireOp",EDGE,"E80.3.0");var subQ2=makeQuery(id+"F36.imprint","INTERSECT",VERTEX,{"disambiguationData":[OD(0.0)],"derivedFrom":[subQ1,subQ0]});Q15=makeQuery(id+"F36.imprint","IMPRINT",FACE,{"disambiguationData":[TD([[makeQuery(id+"F36.imprint","IMPRINT",EDGE,{"disambiguationData":[TD([[subQ2,-1.0]])],"derivedFrom":subQ1}),1.0]])]});}
            extrude(context, id + "F37", {"entities" : qUnion([Q0, Q1, Q2, Q3, Q4, Q5, Q6, Q7, Q8, Q9, Q10, Q11, Q12, Q13, Q14, Q15]), "operationType" : NewBodyOperationType.REMOVE, "oppositeDirection" : true, "depth" : 0.38 * mm, "offsetDistance" : 25.4 * mm});
        }
        {
            var Q0;
            {var subQ0=sQuery(id+"F34.wireOp",EDGE,"E77.3.0");var subQ1=sQuery(id+"F34.wireOp",EDGE,"E77.2.0");var subQ2=sQuery(id+"F34.wireOp",EDGE,"E77.1.0");var subQ3=sQuery(id+"F34.wireOp",EDGE,"E76.0");Q0=makeQuery(id+"F35.boolean.opBoolean","MERGE",FACE,{"derivedFrom":[makeQuery(id+"F7.boolean.opBoolean","MERGE",FACE,{"derivedFrom":[makeQuery(id+"F1.opExtrude","CAP_FACE",FACE,{"disambiguationData":[OSD([sQuery(id+"F0.wireOp",EDGE,"E0.bottom"),sQuery(id+"F0.wireOp",EDGE,"E0.top"),sQuery(id+"F0.wireOp",EDGE,"E0.left"),sQuery(id+"F0.wireOp",EDGE,"E0.right")])],"isStart":true}),makeQuery(id+"F7.opExtrude","CAP_FACE",FACE,{"disambiguationData":[OSD([sQuery(id+"F6.wireOp",EDGE,"E5")])],"isStart":false})]}),makeQuery(id+"F35.opExtrude","CAP_FACE",FACE,{"disambiguationData":[OSD([sQuery(id+"F34.wireOp",EDGE,"E69"),subQ3])],"isStart":false}),makeQuery(id+"F35.opExtrude","CAP_FACE",FACE,{"disambiguationData":[OSD([sQuery(id+"F34.wireOp",EDGE,"E70"),subQ3])],"isStart":false}),makeQuery(id+"F35.opExtrude","CAP_FACE",FACE,{"disambiguationData":[OSD([sQuery(id+"F34.wireOp",EDGE,"E71"),subQ3])],"isStart":false}),makeQuery(id+"F35.opExtrude","CAP_FACE",FACE,{"disambiguationData":[OSD([sQuery(id+"F34.wireOp",EDGE,"E72"),subQ3])],"isStart":false}),makeQuery(id+"F35.opExtrude","CAP_FACE",FACE,{"disambiguationData":[OSD([sQuery(id+"F34.wireOp",EDGE,"E75.1.0"),subQ2])],"isStart":false}),makeQuery(id+"F35.opExtrude","CAP_FACE",FACE,{"disambiguationData":[OSD([sQuery(id+"F34.wireOp",EDGE,"E75.1.1"),subQ2])],"isStart":false}),makeQuery(id+"F35.opExtrude","CAP_FACE",FACE,{"disambiguationData":[OSD([sQuery(id+"F34.wireOp",EDGE,"E75.1.2"),subQ2])],"isStart":false}),makeQuery(id+"F35.opExtrude","CAP_FACE",FACE,{"disambiguationData":[OSD([sQuery(id+"F34.wireOp",EDGE,"E75.1.3"),subQ2])],"isStart":false}),makeQuery(id+"F35.opExtrude","CAP_FACE",FACE,{"disambiguationData":[OSD([sQuery(id+"F34.wireOp",EDGE,"E75.2.0"),subQ1])],"isStart":false}),makeQuery(id+"F35.opExtrude","CAP_FACE",FACE,{"disambiguationData":[OSD([sQuery(id+"F34.wireOp",EDGE,"E75.2.1"),subQ1])],"isStart":false}),makeQuery(id+"F35.opExtrude","CAP_FACE",FACE,{"disambiguationData":[OSD([sQuery(id+"F34.wireOp",EDGE,"E75.2.2"),subQ1])],"isStart":false}),makeQuery(id+"F35.opExtrude","CAP_FACE",FACE,{"disambiguationData":[OSD([sQuery(id+"F34.wireOp",EDGE,"E75.2.3"),subQ1])],"isStart":false}),makeQuery(id+"F35.opExtrude","CAP_FACE",FACE,{"disambiguationData":[OSD([sQuery(id+"F34.wireOp",EDGE,"E75.3.0"),subQ0])],"isStart":false}),makeQuery(id+"F35.opExtrude","CAP_FACE",FACE,{"disambiguationData":[OSD([sQuery(id+"F34.wireOp",EDGE,"E75.3.1"),subQ0])],"isStart":false}),makeQuery(id+"F35.opExtrude","CAP_FACE",FACE,{"disambiguationData":[OSD([sQuery(id+"F34.wireOp",EDGE,"E75.3.2"),subQ0])],"isStart":false}),makeQuery(id+"F35.opExtrude","CAP_FACE",FACE,{"disambiguationData":[OSD([sQuery(id+"F34.wireOp",EDGE,"E75.3.3"),subQ0])],"isStart":false})]});}
            var sketch = newSketch(context, id + "F38", { "sketchPlane" : qUnion([Q0])});
            skCircle(sketch, "E81", {"center": v(8.24, -2.36) * mm, "radius": 2.53 * mm});
            skLineSegment(sketch, "E82.0", {"start": v(5.84, -3.14) * mm, "end": v(7.48, -4.77) * mm});
            skLineSegment(sketch, "E82.1", {"start": v(9.02, -4.76) * mm, "end": v(10.65, -3.13) * mm});
            skLineSegment(sketch, "E82.3", {"start": v(10.65, -1.58) * mm, "end": v(9.01, 0.05) * mm});
            skLineSegment(sketch, "E82.4", {"start": v(7.46, 0.04) * mm, "end": v(5.84, -1.6) * mm});
            skCircle(sketch, "E83.1.0", {"center": v(8.3, 11.52) * mm, "radius": 2.53 * mm});
            skLineSegment(sketch, "E83.1.1", {"start": v(5.9, 10.74) * mm, "end": v(7.54, 9.11) * mm});
            skLineSegment(sketch, "E83.1.2", {"start": v(9.08, 9.12) * mm, "end": v(10.71, 10.75) * mm});
            skLineSegment(sketch, "E83.1.3", {"start": v(10.71, 12.3) * mm, "end": v(9.07, 13.93) * mm});
            skLineSegment(sketch, "E83.1.4", {"start": v(7.53, 13.93) * mm, "end": v(5.9, 12.29) * mm});
            skCircle(sketch, "E83.2.0", {"center": v(-5.57, 11.58) * mm, "radius": 2.53 * mm});
            skLineSegment(sketch, "E83.2.1", {"start": v(-4.8, 9.18) * mm, "end": v(-3.17, 10.82) * mm});
            skLineSegment(sketch, "E83.2.2", {"start": v(-3.17, 12.36) * mm, "end": v(-4.8, 14) * mm});
            skLineSegment(sketch, "E83.2.3", {"start": v(-6.35, 13.99) * mm, "end": v(-7.98, 12.35) * mm});
            skLineSegment(sketch, "E83.2.4", {"start": v(-7.98, 10.8) * mm, "end": v(-6.34, 9.18) * mm});
            skCircle(sketch, "E83.3.0", {"center": v(-5.64, -2.3) * mm, "radius": 2.53 * mm});
            skLineSegment(sketch, "E83.3.1", {"start": v(-3.23, -1.52) * mm, "end": v(-4.87, 0.11) * mm});
            skLineSegment(sketch, "E83.3.2", {"start": v(-6.42, 0.1) * mm, "end": v(-8.05, -1.53) * mm});
            skLineSegment(sketch, "E83.3.3", {"start": v(-8.04, -3.07) * mm, "end": v(-6.4, -4.7) * mm});
            skLineSegment(sketch, "E83.3.4", {"start": v(-4.86, -4.7) * mm, "end": v(-3.23, -3.06) * mm});
            skPoint(sketch, "E83.center", {"position": v(1.33, 4.61) * mm});
            skSolve(sketch);
        }
        {
            var Q0;
            {var subQ0=sQuery(id+"F38.wireOp",EDGE,"E82.3");Q0=makeQuery(id+"F38.imprint","IMPRINT",FACE,{"disambiguationData":[TD([[makeQuery(id+"F38.imprint","IMPRINT",EDGE,{"derivedFrom":subQ0}),-1.0]])]});}
            var Q1;
            {var subQ0=sQuery(id+"F38.wireOp",EDGE,"E82.4");Q1=makeQuery(id+"F38.imprint","IMPRINT",FACE,{"disambiguationData":[TD([[makeQuery(id+"F38.imprint","IMPRINT",EDGE,{"derivedFrom":subQ0}),-1.0]])]});}
            var Q2;
            {var subQ0=sQuery(id+"F38.wireOp",EDGE,"E82.0");Q2=makeQuery(id+"F38.imprint","IMPRINT",FACE,{"disambiguationData":[TD([[makeQuery(id+"F38.imprint","IMPRINT",EDGE,{"derivedFrom":subQ0}),-1.0]])]});}
            var Q3;
            {var subQ0=sQuery(id+"F38.wireOp",EDGE,"E82.1");Q3=makeQuery(id+"F38.imprint","IMPRINT",FACE,{"disambiguationData":[TD([[makeQuery(id+"F38.imprint","IMPRINT",EDGE,{"derivedFrom":subQ0}),-1.0]])]});}
            var Q4;
            {var subQ0=sQuery(id+"F38.wireOp",EDGE,"E83.1.4");Q4=makeQuery(id+"F38.imprint","IMPRINT",FACE,{"disambiguationData":[TD([[makeQuery(id+"F38.imprint","IMPRINT",EDGE,{"derivedFrom":subQ0}),-1.0]])]});}
            var Q5;
            {var subQ0=sQuery(id+"F38.wireOp",EDGE,"E83.1.1");Q5=makeQuery(id+"F38.imprint","IMPRINT",FACE,{"disambiguationData":[TD([[makeQuery(id+"F38.imprint","IMPRINT",EDGE,{"derivedFrom":subQ0}),-1.0]])]});}
            var Q6;
            {var subQ0=sQuery(id+"F38.wireOp",EDGE,"E83.1.2");Q6=makeQuery(id+"F38.imprint","IMPRINT",FACE,{"disambiguationData":[TD([[makeQuery(id+"F38.imprint","IMPRINT",EDGE,{"derivedFrom":subQ0}),-1.0]])]});}
            var Q7;
            {var subQ0=sQuery(id+"F38.wireOp",EDGE,"E83.1.3");Q7=makeQuery(id+"F38.imprint","IMPRINT",FACE,{"disambiguationData":[TD([[makeQuery(id+"F38.imprint","IMPRINT",EDGE,{"derivedFrom":subQ0}),-1.0]])]});}
            var Q8;
            {var subQ0=sQuery(id+"F38.wireOp",EDGE,"E83.2.4");Q8=makeQuery(id+"F38.imprint","IMPRINT",FACE,{"disambiguationData":[TD([[makeQuery(id+"F38.imprint","IMPRINT",EDGE,{"derivedFrom":subQ0}),-1.0]])]});}
            var Q9;
            {var subQ0=sQuery(id+"F38.wireOp",EDGE,"E83.2.1");Q9=makeQuery(id+"F38.imprint","IMPRINT",FACE,{"disambiguationData":[TD([[makeQuery(id+"F38.imprint","IMPRINT",EDGE,{"derivedFrom":subQ0}),-1.0]])]});}
            var Q10;
            {var subQ0=sQuery(id+"F38.wireOp",EDGE,"E83.2.2");Q10=makeQuery(id+"F38.imprint","IMPRINT",FACE,{"disambiguationData":[TD([[makeQuery(id+"F38.imprint","IMPRINT",EDGE,{"derivedFrom":subQ0}),-1.0]])]});}
            var Q11;
            {var subQ0=sQuery(id+"F38.wireOp",EDGE,"E83.2.3");Q11=makeQuery(id+"F38.imprint","IMPRINT",FACE,{"disambiguationData":[TD([[makeQuery(id+"F38.imprint","IMPRINT",EDGE,{"derivedFrom":subQ0}),-1.0]])]});}
            var Q12;
            {var subQ0=sQuery(id+"F38.wireOp",EDGE,"E83.3.4");Q12=makeQuery(id+"F38.imprint","IMPRINT",FACE,{"disambiguationData":[TD([[makeQuery(id+"F38.imprint","IMPRINT",EDGE,{"derivedFrom":subQ0}),-1.0]])]});}
            var Q13;
            {var subQ0=sQuery(id+"F38.wireOp",EDGE,"E83.3.1");Q13=makeQuery(id+"F38.imprint","IMPRINT",FACE,{"disambiguationData":[TD([[makeQuery(id+"F38.imprint","IMPRINT",EDGE,{"derivedFrom":subQ0}),-1.0]])]});}
            var Q14;
            {var subQ0=sQuery(id+"F38.wireOp",EDGE,"E83.3.2");Q14=makeQuery(id+"F38.imprint","IMPRINT",FACE,{"disambiguationData":[TD([[makeQuery(id+"F38.imprint","IMPRINT",EDGE,{"derivedFrom":subQ0}),-1.0]])]});}
            var Q15;
            {var subQ0=sQuery(id+"F38.wireOp",EDGE,"E83.3.3");Q15=makeQuery(id+"F38.imprint","IMPRINT",FACE,{"disambiguationData":[TD([[makeQuery(id+"F38.imprint","IMPRINT",EDGE,{"derivedFrom":subQ0}),-1.0]])]});}
            extrude(context, id + "F39", {"entities" : qUnion([Q0, Q1, Q2, Q3, Q4, Q5, Q6, Q7, Q8, Q9, Q10, Q11, Q12, Q13, Q14, Q15]), "operationType" : NewBodyOperationType.REMOVE, "oppositeDirection" : true, "depth" : 0.38 * mm, "offsetDistance" : 25.4 * mm});
        }
        {
            var Q0;
            {var subQ0=sQuery(id+"F34.wireOp",EDGE,"E77.3.0");var subQ1=sQuery(id+"F34.wireOp",EDGE,"E77.2.0");var subQ2=sQuery(id+"F34.wireOp",EDGE,"E77.1.0");var subQ3=sQuery(id+"F34.wireOp",EDGE,"E76.0");Q0=makeQuery(id+"F35.boolean.opBoolean","MERGE",FACE,{"derivedFrom":[makeQuery(id+"F9.boolean.opBoolean","MERGE",FACE,{"derivedFrom":[makeQuery(id+"F1.opExtrude","CAP_FACE",FACE,{"disambiguationData":[OSD([sQuery(id+"F0.wireOp",EDGE,"E0.bottom"),sQuery(id+"F0.wireOp",EDGE,"E0.top"),sQuery(id+"F0.wireOp",EDGE,"E0.left"),sQuery(id+"F0.wireOp",EDGE,"E0.right")])],"isStart":false}),makeQuery(id+"F9.opExtrude","CAP_FACE",FACE,{"disambiguationData":[OSD([sQuery(id+"F8.wireOp",EDGE,"E8")])],"isStart":false})]}),makeQuery(id+"F35.opExtrude","CAP_FACE",FACE,{"disambiguationData":[OSD([sQuery(id+"F34.wireOp",EDGE,"E69"),subQ3])],"isStart":true}),makeQuery(id+"F35.opExtrude","CAP_FACE",FACE,{"disambiguationData":[OSD([sQuery(id+"F34.wireOp",EDGE,"E70"),subQ3])],"isStart":true}),makeQuery(id+"F35.opExtrude","CAP_FACE",FACE,{"disambiguationData":[OSD([sQuery(id+"F34.wireOp",EDGE,"E71"),subQ3])],"isStart":true}),makeQuery(id+"F35.opExtrude","CAP_FACE",FACE,{"disambiguationData":[OSD([sQuery(id+"F34.wireOp",EDGE,"E72"),subQ3])],"isStart":true}),makeQuery(id+"F35.opExtrude","CAP_FACE",FACE,{"disambiguationData":[OSD([sQuery(id+"F34.wireOp",EDGE,"E75.1.0"),subQ2])],"isStart":true}),makeQuery(id+"F35.opExtrude","CAP_FACE",FACE,{"disambiguationData":[OSD([sQuery(id+"F34.wireOp",EDGE,"E75.1.1"),subQ2])],"isStart":true}),makeQuery(id+"F35.opExtrude","CAP_FACE",FACE,{"disambiguationData":[OSD([sQuery(id+"F34.wireOp",EDGE,"E75.1.2"),subQ2])],"isStart":true}),makeQuery(id+"F35.opExtrude","CAP_FACE",FACE,{"disambiguationData":[OSD([sQuery(id+"F34.wireOp",EDGE,"E75.1.3"),subQ2])],"isStart":true}),makeQuery(id+"F35.opExtrude","CAP_FACE",FACE,{"disambiguationData":[OSD([sQuery(id+"F34.wireOp",EDGE,"E75.2.0"),subQ1])],"isStart":true}),makeQuery(id+"F35.opExtrude","CAP_FACE",FACE,{"disambiguationData":[OSD([sQuery(id+"F34.wireOp",EDGE,"E75.2.1"),subQ1])],"isStart":true}),makeQuery(id+"F35.opExtrude","CAP_FACE",FACE,{"disambiguationData":[OSD([sQuery(id+"F34.wireOp",EDGE,"E75.2.2"),subQ1])],"isStart":true}),makeQuery(id+"F35.opExtrude","CAP_FACE",FACE,{"disambiguationData":[OSD([sQuery(id+"F34.wireOp",EDGE,"E75.2.3"),subQ1])],"isStart":true}),makeQuery(id+"F35.opExtrude","CAP_FACE",FACE,{"disambiguationData":[OSD([sQuery(id+"F34.wireOp",EDGE,"E75.3.0"),subQ0])],"isStart":true}),makeQuery(id+"F35.opExtrude","CAP_FACE",FACE,{"disambiguationData":[OSD([sQuery(id+"F34.wireOp",EDGE,"E75.3.1"),subQ0])],"isStart":true}),makeQuery(id+"F35.opExtrude","CAP_FACE",FACE,{"disambiguationData":[OSD([sQuery(id+"F34.wireOp",EDGE,"E75.3.2"),subQ0])],"isStart":true}),makeQuery(id+"F35.opExtrude","CAP_FACE",FACE,{"disambiguationData":[OSD([sQuery(id+"F34.wireOp",EDGE,"E75.3.3"),subQ0])],"isStart":true})]});}
            extrude(context, id + "F40", {"entities" : qUnion([Q0]), "operationType" : NewBodyOperationType.ADD, "depth" : 12.2 * mm, "offsetDistance" : 25 * mm});
        }
        {
            var Q0;
            {var subQ0=sQuery(id+"F0.wireOp",EDGE,"E0.left");Q0=makeQuery(id+"F40.boolean.opBoolean","MERGE",FACE,{"derivedFrom":[makeQuery(id+"F1.opExtrude","SWEPT_FACE",FACE,{"disambiguationData":[OSD([subQ0])]}),makeQuery(id+"F40.opExtrude","SWEPT_FACE",FACE,{"disambiguationData":[OSD([subQ0])]})]});}
            var sketch = newSketch(context, id + "F41", { "sketchPlane" : qUnion([Q0])});
            skCircle(sketch, "E84.0", {"center": v(-2.33, 6.9) * mm, "radius": 2.53 * mm});
            skLineSegment(sketch, "E84.1", {"start": v(-4.58, 8.05) * mm, "end": v(-4.58, 5.74) * mm});
            skLineSegment(sketch, "E84.2", {"start": v(-3.48, 4.65) * mm, "end": v(-1.17, 4.65) * mm});
            skLineSegment(sketch, "E84.3", {"start": v(-1.17, 9.14) * mm, "end": v(-3.48, 9.14) * mm});
            skLineSegment(sketch, "E84.4", {"start": v(-0.08, 5.74) * mm, "end": v(-0.08, 8.05) * mm});
            skPoint(sketch, "E85", {"position": v(11.55, 6.9) * mm});
            skLineSegment(sketch, "E86.0.1.0", {"start": v(-4.58, 20.25) * mm, "end": v(-4.58, 17.94) * mm});
            skCircle(sketch, "E86.0.1.1", {"center": v(-2.33, 19.1) * mm, "radius": 2.53 * mm});
            skLineSegment(sketch, "E86.0.1.2", {"start": v(-1.17, 21.34) * mm, "end": v(-3.48, 21.34) * mm});
            skLineSegment(sketch, "E86.0.1.3", {"start": v(-0.08, 17.94) * mm, "end": v(-0.08, 20.25) * mm});
            skLineSegment(sketch, "E86.0.1.4", {"start": v(-3.48, 16.85) * mm, "end": v(-1.17, 16.85) * mm});
            skLineSegment(sketch, "E86.1.0.0", {"start": v(9.3, 8.05) * mm, "end": v(9.3, 5.74) * mm});
            skCircle(sketch, "E86.1.0.1", {"center": v(11.55, 6.9) * mm, "radius": 2.53 * mm});
            skLineSegment(sketch, "E86.1.0.2", {"start": v(12.7, 9.14) * mm, "end": v(10.4, 9.14) * mm});
            skLineSegment(sketch, "E86.1.0.3", {"start": v(13.8, 5.74) * mm, "end": v(13.8, 8.05) * mm});
            skLineSegment(sketch, "E86.1.0.4", {"start": v(10.4, 4.65) * mm, "end": v(12.7, 4.65) * mm});
            skLineSegment(sketch, "E86.1.1.0", {"start": v(9.3, 20.25) * mm, "end": v(9.3, 17.94) * mm});
            skCircle(sketch, "E86.1.1.1", {"center": v(11.55, 19.1) * mm, "radius": 2.53 * mm});
            skLineSegment(sketch, "E86.1.1.2", {"start": v(12.7, 21.34) * mm, "end": v(10.4, 21.34) * mm});
            skLineSegment(sketch, "E86.1.1.3", {"start": v(13.8, 17.94) * mm, "end": v(13.8, 20.25) * mm});
            skLineSegment(sketch, "E86.1.1.4", {"start": v(10.4, 16.85) * mm, "end": v(12.7, 16.85) * mm});
            skLineSegment(sketch, "E86.direction1", {"start": v(-4.58, 5.74) * mm, "end": v(9.3, 5.74) * mm, "construction": true});
            skLineSegment(sketch, "E86.direction2", {"start": v(-4.58, 5.74) * mm, "end": v(-4.58, 17.94) * mm, "construction": true});
            skLineSegment(sketch, "E87", {"start": v(-9.27, 13) * mm, "end": v(18.5, 13) * mm, "construction": true});
            skLineSegment(sketch, "E88", {"start": v(-2.33, 19.1) * mm, "end": v(-2.33, 6.9) * mm, "construction": true});
            skPoint(sketch, "E89", {"position": v(-2.33, 13) * mm});
            skSolve(sketch);
        }
        {
            var Q0;
            {var subQ1=sQuery(id+"F41.wireOp",EDGE,"E86.1.1.0");Q0=makeQuery(id+"F41.imprint","IMPRINT",FACE,{"disambiguationData":[TD([[makeQuery(id+"F41.imprint","IMPRINT",EDGE,{"derivedFrom":subQ1}),1.0]])]});}
            var Q1;
            {var subQ1=sQuery(id+"F41.wireOp",EDGE,"E86.0.1.0");Q1=makeQuery(id+"F41.imprint","IMPRINT",FACE,{"disambiguationData":[TD([[makeQuery(id+"F41.imprint","IMPRINT",EDGE,{"derivedFrom":subQ1}),1.0]])]});}
            extrude(context, id + "F42", {"entities" : qUnion([Q0, Q1]), "operationType" : NewBodyOperationType.REMOVE, "oppositeDirection" : true, "depth" : 6.9 * mm, "offsetDistance" : 25 * mm});
        }
        {
            var Q0;
            {var subQ0=sQuery(id+"F41.wireOp",EDGE,"E86.1.1.4");Q0=makeQuery(id+"F41.imprint","IMPRINT",FACE,{"disambiguationData":[TD([[makeQuery(id+"F41.imprint","IMPRINT",EDGE,{"derivedFrom":subQ0}),-1.0]])]});}
            var Q1;
            {var subQ0=sQuery(id+"F41.wireOp",EDGE,"E86.1.1.3");Q1=makeQuery(id+"F41.imprint","IMPRINT",FACE,{"disambiguationData":[TD([[makeQuery(id+"F41.imprint","IMPRINT",EDGE,{"derivedFrom":subQ0}),-1.0]])]});}
            var Q2;
            {var subQ0=sQuery(id+"F41.wireOp",EDGE,"E86.1.1.0");Q2=makeQuery(id+"F41.imprint","IMPRINT",FACE,{"disambiguationData":[TD([[makeQuery(id+"F41.imprint","IMPRINT",EDGE,{"derivedFrom":subQ0}),-1.0]])]});}
            var Q3;
            {var subQ0=sQuery(id+"F41.wireOp",EDGE,"E86.1.1.2");Q3=makeQuery(id+"F41.imprint","IMPRINT",FACE,{"disambiguationData":[TD([[makeQuery(id+"F41.imprint","IMPRINT",EDGE,{"derivedFrom":subQ0}),-1.0]])]});}
            var Q4;
            {var subQ0=sQuery(id+"F41.wireOp",EDGE,"E86.0.1.4");Q4=makeQuery(id+"F41.imprint","IMPRINT",FACE,{"disambiguationData":[TD([[makeQuery(id+"F41.imprint","IMPRINT",EDGE,{"derivedFrom":subQ0}),-1.0]])]});}
            var Q5;
            {var subQ0=sQuery(id+"F41.wireOp",EDGE,"E86.0.1.3");Q5=makeQuery(id+"F41.imprint","IMPRINT",FACE,{"disambiguationData":[TD([[makeQuery(id+"F41.imprint","IMPRINT",EDGE,{"derivedFrom":subQ0}),-1.0]])]});}
            var Q6;
            {var subQ0=sQuery(id+"F41.wireOp",EDGE,"E86.0.1.2");Q6=makeQuery(id+"F41.imprint","IMPRINT",FACE,{"disambiguationData":[TD([[makeQuery(id+"F41.imprint","IMPRINT",EDGE,{"derivedFrom":subQ0}),-1.0]])]});}
            var Q7;
            {var subQ0=sQuery(id+"F41.wireOp",EDGE,"E86.0.1.0");Q7=makeQuery(id+"F41.imprint","IMPRINT",FACE,{"disambiguationData":[TD([[makeQuery(id+"F41.imprint","IMPRINT",EDGE,{"derivedFrom":subQ0}),-1.0]])]});}
            extrude(context, id + "F43", {"entities" : qUnion([Q0, Q1, Q2, Q3, Q4, Q5, Q6, Q7]), "operationType" : NewBodyOperationType.REMOVE, "oppositeDirection" : true, "depth" : 0.2 * mm, "offsetDistance" : 25 * mm});
        }
        {
            var Q0;
            {var subQ0=sQuery(id+"F0.wireOp",EDGE,"E0.right");Q0=makeQuery(id+"F40.boolean.opBoolean","MERGE",FACE,{"derivedFrom":[makeQuery(id+"F1.opExtrude","SWEPT_FACE",FACE,{"disambiguationData":[OSD([subQ0])]}),makeQuery(id+"F40.opExtrude","SWEPT_FACE",FACE,{"disambiguationData":[OSD([subQ0])]})]});}
            var sketch = newSketch(context, id + "F44", { "sketchPlane" : qUnion([Q0])});
            skCircle(sketch, "E90.0", {"center": v(-11.55, 19.1) * mm, "radius": 2.53 * mm});
            skLineSegment(sketch, "E90.1", {"start": v(-10.4, 16.85) * mm, "end": v(-12.7, 16.85) * mm});
            skLineSegment(sketch, "E90.2", {"start": v(-13.8, 17.94) * mm, "end": v(-13.8, 20.25) * mm});
            skLineSegment(sketch, "E90.3", {"start": v(-12.7, 21.34) * mm, "end": v(-10.4, 21.34) * mm});
            skLineSegment(sketch, "E90.4", {"start": v(-9.3, 20.25) * mm, "end": v(-9.3, 17.94) * mm});
            skCircle(sketch, "E90.5", {"center": v(2.33, 19.1) * mm, "radius": 2.53 * mm});
            skLineSegment(sketch, "E90.6", {"start": v(3.48, 16.85) * mm, "end": v(1.17, 16.85) * mm});
            skLineSegment(sketch, "E90.7", {"start": v(0.08, 17.94) * mm, "end": v(0.08, 20.25) * mm});
            skLineSegment(sketch, "E90.8", {"start": v(1.17, 21.34) * mm, "end": v(3.48, 21.34) * mm});
            skLineSegment(sketch, "E90.9", {"start": v(4.58, 20.25) * mm, "end": v(4.58, 17.94) * mm});
            skSolve(sketch);
        }
        {
            var Q0;
            {var subQ0=sQuery(id+"F44.wireOp",EDGE,"E90.1");Q0=makeQuery(id+"F44.imprint","IMPRINT",FACE,{"disambiguationData":[TD([[makeQuery(id+"F44.imprint","IMPRINT",EDGE,{"derivedFrom":subQ0}),-1.0]])]});}
            var Q1;
            {var subQ0=sQuery(id+"F44.wireOp",EDGE,"E90.6");Q1=makeQuery(id+"F44.imprint","IMPRINT",FACE,{"disambiguationData":[TD([[makeQuery(id+"F44.imprint","IMPRINT",EDGE,{"derivedFrom":subQ0}),-1.0]])]});}
            extrude(context, id + "F45", {"entities" : qUnion([Q0, Q1]), "operationType" : NewBodyOperationType.REMOVE, "oppositeDirection" : true, "depth" : 6.7 * mm, "offsetDistance" : 25 * mm});
        }
        {
            var Q0;
            {var subQ0=sQuery(id+"F44.wireOp",EDGE,"E90.3");Q0=makeQuery(id+"F44.imprint","IMPRINT",FACE,{"disambiguationData":[TD([[makeQuery(id+"F44.imprint","IMPRINT",EDGE,{"derivedFrom":subQ0}),1.0]])]});}
            var Q1;
            {var subQ0=sQuery(id+"F44.wireOp",EDGE,"E90.2");Q1=makeQuery(id+"F44.imprint","IMPRINT",FACE,{"disambiguationData":[TD([[makeQuery(id+"F44.imprint","IMPRINT",EDGE,{"derivedFrom":subQ0}),1.0]])]});}
            var Q2;
            {var subQ0=sQuery(id+"F44.wireOp",EDGE,"E90.1");Q2=makeQuery(id+"F44.imprint","IMPRINT",FACE,{"disambiguationData":[TD([[makeQuery(id+"F44.imprint","IMPRINT",EDGE,{"derivedFrom":subQ0}),1.0]])]});}
            var Q3;
            {var subQ0=sQuery(id+"F44.wireOp",EDGE,"E90.4");Q3=makeQuery(id+"F44.imprint","IMPRINT",FACE,{"disambiguationData":[TD([[makeQuery(id+"F44.imprint","IMPRINT",EDGE,{"derivedFrom":subQ0}),1.0]])]});}
            var Q4;
            {var subQ0=sQuery(id+"F44.wireOp",EDGE,"E90.7");Q4=makeQuery(id+"F44.imprint","IMPRINT",FACE,{"disambiguationData":[TD([[makeQuery(id+"F44.imprint","IMPRINT",EDGE,{"derivedFrom":subQ0}),1.0]])]});}
            var Q5;
            {var subQ0=sQuery(id+"F44.wireOp",EDGE,"E90.8");Q5=makeQuery(id+"F44.imprint","IMPRINT",FACE,{"disambiguationData":[TD([[makeQuery(id+"F44.imprint","IMPRINT",EDGE,{"derivedFrom":subQ0}),1.0]])]});}
            var Q6;
            {var subQ0=sQuery(id+"F44.wireOp",EDGE,"E90.9");Q6=makeQuery(id+"F44.imprint","IMPRINT",FACE,{"disambiguationData":[TD([[makeQuery(id+"F44.imprint","IMPRINT",EDGE,{"derivedFrom":subQ0}),1.0]])]});}
            var Q7;
            {var subQ0=sQuery(id+"F44.wireOp",EDGE,"E90.6");Q7=makeQuery(id+"F44.imprint","IMPRINT",FACE,{"disambiguationData":[TD([[makeQuery(id+"F44.imprint","IMPRINT",EDGE,{"derivedFrom":subQ0}),1.0]])]});}
            extrude(context, id + "F46", {"entities" : qUnion([Q0, Q1, Q2, Q3, Q4, Q5, Q6, Q7]), "operationType" : NewBodyOperationType.REMOVE, "oppositeDirection" : true, "depth" : 0.16 * mm, "offsetDistance" : 25 * mm});
        }
        {
            var Q0;
            {var subQ0=sQuery(id+"F0.wireOp",EDGE,"E0.top");var subQ2=sQuery(id+"F0.wireOp",EDGE,"E0.left");Q0=makeQuery(id+"F40.boolean.opBoolean","MERGE",FACE,{"derivedFrom":[makeQuery(id+"F21.boolean.opBoolean","SPLIT",FACE,{"disambiguationData":[TD([makeQuery(id+"F1.opExtrude","SWEPT_FACE",FACE,{"disambiguationData":[OSD([subQ2])]})])],"derivedFrom":makeQuery(id+"F1.opExtrude","SWEPT_FACE",FACE,{"disambiguationData":[OSD([subQ0])]})}),makeQuery(id+"F40.opExtrude","SWEPT_FACE",FACE,{"disambiguationData":[OSD([subQ0])]})]});}
            var sketch = newSketch(context, id + "F47", { "sketchPlane" : qUnion([Q0])});
            skCircle(sketch, "E91.0", {"center": v(-5.64, 6.9) * mm, "radius": 2.26 * mm});
            skCircle(sketch, "E91.1", {"center": v(-5.64, 6.9) * mm, "radius": 1.04 * mm});
            skCircle(sketch, "E92.0.1.0", {"center": v(-5.64, 19.1) * mm, "radius": 2.26 * mm});
            skCircle(sketch, "E92.0.1.1", {"center": v(-5.64, 19.1) * mm, "radius": 1.04 * mm});
            skCircle(sketch, "E92.1.0.0", {"center": v(8.24, 6.9) * mm, "radius": 2.26 * mm});
            skCircle(sketch, "E92.1.0.1", {"center": v(8.24, 6.9) * mm, "radius": 1.04 * mm});
            skCircle(sketch, "E92.1.1.0", {"center": v(8.24, 19.1) * mm, "radius": 2.26 * mm});
            skCircle(sketch, "E92.1.1.1", {"center": v(8.24, 19.1) * mm, "radius": 1.04 * mm});
            skLineSegment(sketch, "E92.direction1", {"start": v(-5.64, 6.9) * mm, "end": v(8.24, 6.9) * mm, "construction": true});
            skLineSegment(sketch, "E92.direction2", {"start": v(-5.64, 6.9) * mm, "end": v(-5.64, 19.1) * mm, "construction": true});
            skLineSegment(sketch, "E93", {"start": v(-12.61, 13) * mm, "end": v(15.28, 13) * mm, "construction": true});
            skPoint(sketch, "E94", {"position": v(-5.64, 13) * mm});
            skSolve(sketch);
        }
        {
            var Q0;
            Q0 = qSketchRegion(id + "F47", true);
            extrude(context, id + "F48", {"entities" : qUnion([Q0]), "operationType" : NewBodyOperationType.ADD, "depth" : 3.78 * mm, "offsetDistance" : 25 * mm});
        }
        {
            var Q0;
            {var subQ0=sQuery(id+"F0.wireOp",EDGE,"E0.bottom");Q0=makeQuery(id+"F40.boolean.opBoolean","MERGE",FACE,{"derivedFrom":[makeQuery(id+"F1.opExtrude","SWEPT_FACE",FACE,{"disambiguationData":[OSD([subQ0])]}),makeQuery(id+"F40.opExtrude","SWEPT_FACE",FACE,{"disambiguationData":[OSD([subQ0])]})]});}
            var sketch = newSketch(context, id + "F49", { "sketchPlane" : qUnion([Q0])});
            skCircle(sketch, "E95.0", {"center": v(-8.23, 6.9) * mm, "radius": 2.53 * mm});
            skLineSegment(sketch, "E95.1", {"start": v(-10.48, 8.05) * mm, "end": v(-10.48, 5.74) * mm});
            skLineSegment(sketch, "E95.2", {"start": v(-7.08, 4.65) * mm, "end": v(-9.39, 4.65) * mm});
            skLineSegment(sketch, "E95.3", {"start": v(-5.98, 8.05) * mm, "end": v(-5.98, 5.74) * mm});
            skLineSegment(sketch, "E95.4", {"start": v(-7.08, 9.14) * mm, "end": v(-9.39, 9.14) * mm});
            skCircle(sketch, "E96.0.1.0", {"center": v(-8.23, 19.1) * mm, "radius": 2.53 * mm});
            skLineSegment(sketch, "E96.0.1.1", {"start": v(-7.08, 21.34) * mm, "end": v(-9.39, 21.34) * mm});
            skLineSegment(sketch, "E96.0.1.2", {"start": v(-10.48, 20.25) * mm, "end": v(-10.48, 17.94) * mm});
            skLineSegment(sketch, "E96.0.1.3", {"start": v(-7.08, 16.85) * mm, "end": v(-9.39, 16.85) * mm});
            skLineSegment(sketch, "E96.0.1.4", {"start": v(-5.98, 20.25) * mm, "end": v(-5.98, 17.94) * mm});
            skCircle(sketch, "E96.1.0.0", {"center": v(5.65, 6.9) * mm, "radius": 2.53 * mm});
            skLineSegment(sketch, "E96.1.0.1", {"start": v(6.8, 9.14) * mm, "end": v(4.5, 9.14) * mm});
            skLineSegment(sketch, "E96.1.0.2", {"start": v(3.4, 8.05) * mm, "end": v(3.4, 5.74) * mm});
            skLineSegment(sketch, "E96.1.0.3", {"start": v(6.8, 4.65) * mm, "end": v(4.5, 4.65) * mm});
            skLineSegment(sketch, "E96.1.0.4", {"start": v(7.9, 8.05) * mm, "end": v(7.9, 5.74) * mm});
            skCircle(sketch, "E96.1.1.0", {"center": v(5.65, 19.1) * mm, "radius": 2.53 * mm});
            skLineSegment(sketch, "E96.1.1.1", {"start": v(6.8, 21.34) * mm, "end": v(4.5, 21.34) * mm});
            skLineSegment(sketch, "E96.1.1.2", {"start": v(3.4, 20.25) * mm, "end": v(3.4, 17.94) * mm});
            skLineSegment(sketch, "E96.1.1.3", {"start": v(6.8, 16.85) * mm, "end": v(4.5, 16.85) * mm});
            skLineSegment(sketch, "E96.1.1.4", {"start": v(7.9, 20.25) * mm, "end": v(7.9, 17.94) * mm});
            skLineSegment(sketch, "E96.direction1", {"start": v(-8.23, 6.9) * mm, "end": v(5.65, 6.9) * mm, "construction": true});
            skLineSegment(sketch, "E96.direction2", {"start": v(-8.23, 6.9) * mm, "end": v(-8.23, 19.1) * mm, "construction": true});
            skLineSegment(sketch, "E97", {"start": v(-15.28, 13) * mm, "end": v(12.61, 13) * mm, "construction": true});
            skPoint(sketch, "E98", {"position": v(-8.23, 13) * mm});
            skSolve(sketch);
        }
        {
            var Q0;
            Q0 = qSketchRegion(id + "F49", true);
            extrude(context, id + "F50", {"entities" : qUnion([Q0]), "operationType" : NewBodyOperationType.REMOVE, "oppositeDirection" : true, "depth" : 8.2 * mm, "offsetDistance" : 25 * mm});
        }
    });
